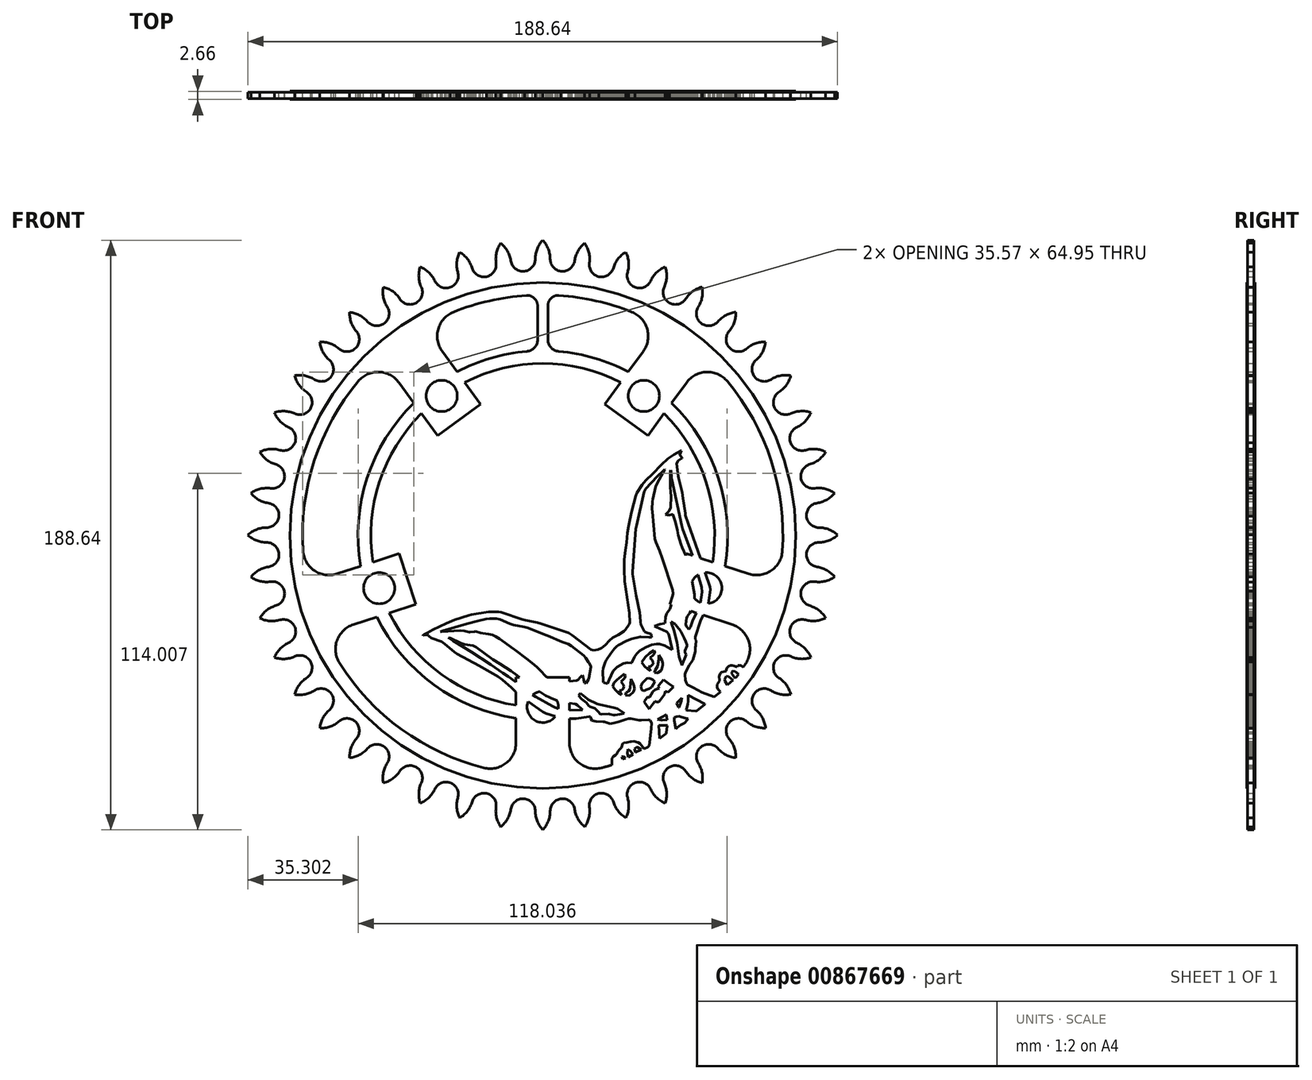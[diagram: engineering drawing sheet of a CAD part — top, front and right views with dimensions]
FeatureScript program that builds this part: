
annotation { "Feature Type Name" : "Feature", "Feature Type Description" : "" }
export const myFeature = defineFeature(function(context is Context, id is Id, definition is map)
    precondition{}
    {
        {
            var Q0;
            Q0=qCreatedBy(makeId("Front.planeOp"),FACE);
            var sketch = newSketch(context, id + "F0", { "sketchPlane" : qUnion([Q0])});
            skArc(sketch, "E0", {"start": v(-6.35, 84.36) * mm, "mid": v(-3.54, 85.52) * mm, "end": v(-2.38, 88.33) * mm});
            skArc(sketch, "E1.MirrorC", {"start": v(6.35, 84.36) * mm, "mid": v(3.54, 85.53) * mm, "end": v(2.38, 88.33) * mm});
            skPoint(sketch, "E2.orphan", {"position": v(12.57, 87.43) * mm});
            skPoint(sketch, "E3.trimOffspring.end.orphan", {"position": v(-12.57, 87.43) * mm});
            skLineSegment(sketch, "E4.trimOffspring", {"start": v(-5.78, 84.4) * mm, "end": v(-5.79, 84.4) * mm});
            skLineSegment(sketch, "E5.trimOffspring", {"start": v(5.78, 84.4) * mm, "end": v(5.79, 84.4) * mm});
            skPoint(sketch, "E6.MirrorCS.start.orphan", {"position": v(6.35, 0) * mm});
            skPoint(sketch, "E7.start.orphan", {"position": v(-6.35, 0) * mm});
            skArc(sketch, "E8.trimOffspring", {"start": v(-2.38, 88.33) * mm, "mid": v(-1.77, 91.55) * mm, "end": v(-0.01, 94.32) * mm});
            skPoint(sketch, "E9.trimOffspring.end.orphan", {"position": v(0, 88.33) * mm});
            skArc(sketch, "E10.trimOffspring", {"start": v(2.38, 88.33) * mm, "mid": v(1.76, 91.56) * mm, "end": v(-0.01, 94.32) * mm});
            skArc(sketch, "E11.1.0", {"start": v(-10.21, 87.77) * mm, "mid": v(-11.3, 90.88) * mm, "end": v(-13.44, 93.36) * mm});
            skPoint(sketch, "E11.1.2", {"position": v(-18.86, 86.53) * mm});
            skPoint(sketch, "E11.1.3", {"position": v(-6.29, 88.34) * mm});
            skArc(sketch, "E11.1.4", {"start": v(-14.93, 87.1) * mm, "mid": v(-14.78, 90.37) * mm, "end": v(-13.44, 93.36) * mm});
            skArc(sketch, "E11.1.5", {"start": v(-5.72, 84.4) * mm, "mid": v(-8.67, 85.16) * mm, "end": v(-10.21, 87.77) * mm});
            skArc(sketch, "E11.1.6", {"start": v(-18.3, 82.6) * mm, "mid": v(-15.68, 84.15) * mm, "end": v(-14.93, 87.1) * mm});
            skArc(sketch, "E11.2.0", {"start": v(-22.6, 85.43) * mm, "mid": v(-24.1, 88.34) * mm, "end": v(-26.59, 90.5) * mm});
            skPoint(sketch, "E11.2.1", {"position": v(-24.88, 84.75) * mm});
            skPoint(sketch, "E11.2.2", {"position": v(-30.98, 82.96) * mm});
            skPoint(sketch, "E11.2.3", {"position": v(-18.8, 86.54) * mm});
            skArc(sketch, "E11.2.4", {"start": v(-27.17, 84.08) * mm, "mid": v(-27.5, 87.35) * mm, "end": v(-26.59, 90.5) * mm});
            skArc(sketch, "E11.2.5", {"start": v(-17.67, 82.73) * mm, "mid": v(-20.7, 83.06) * mm, "end": v(-22.6, 85.43) * mm});
            skArc(sketch, "E11.2.6", {"start": v(-29.86, 79.16) * mm, "mid": v(-27.5, 81.06) * mm, "end": v(-27.17, 84.08) * mm});
            skArc(sketch, "E11.3.0", {"start": v(-34.53, 81.34) * mm, "mid": v(-36.43, 84.01) * mm, "end": v(-39.2, 85.8) * mm});
            skPoint(sketch, "E11.3.1", {"position": v(-36.7, 80.35) * mm});
            skPoint(sketch, "E11.3.2", {"position": v(-42.47, 77.71) * mm});
            skPoint(sketch, "E11.3.3", {"position": v(-30.92, 82.99) * mm});
            skArc(sketch, "E11.3.4", {"start": v(-38.86, 79.36) * mm, "mid": v(-39.64, 82.54) * mm, "end": v(-39.2, 85.8) * mm});
            skArc(sketch, "E11.3.5", {"start": v(-29.27, 79.38) * mm, "mid": v(-32.3, 79.27) * mm, "end": v(-34.53, 81.34) * mm});
            skArc(sketch, "E11.3.6", {"start": v(-40.82, 74.1) * mm, "mid": v(-38.75, 76.32) * mm, "end": v(-38.86, 79.36) * mm});
            skArc(sketch, "E11.4.0", {"start": v(-45.75, 75.6) * mm, "mid": v(-48.02, 77.97) * mm, "end": v(-51, 79.34) * mm});
            skPoint(sketch, "E11.4.1", {"position": v(-47.75, 74.3) * mm});
            skPoint(sketch, "E11.4.2", {"position": v(-53.1, 70.88) * mm});
            skPoint(sketch, "E11.4.3", {"position": v(-42.41, 77.74) * mm});
            skArc(sketch, "E11.4.4", {"start": v(-49.76, 73.02) * mm, "mid": v(-50.98, 76.06) * mm, "end": v(-51, 79.34) * mm});
            skArc(sketch, "E11.4.5", {"start": v(-40.27, 74.4) * mm, "mid": v(-43.26, 73.86) * mm, "end": v(-45.75, 75.6) * mm});
            skArc(sketch, "E11.4.6", {"start": v(-50.95, 67.54) * mm, "mid": v(-49.22, 70.03) * mm, "end": v(-49.76, 73.02) * mm});
            skArc(sketch, "E11.5.0", {"start": v(-56.05, 68.32) * mm, "mid": v(-58.63, 70.35) * mm, "end": v(-61.78, 71.28) * mm});
            skPoint(sketch, "E11.5.1", {"position": v(-57.84, 66.76) * mm});
            skPoint(sketch, "E11.5.2", {"position": v(-62.64, 62.6) * mm});
            skPoint(sketch, "E11.5.3", {"position": v(-53.04, 70.91) * mm});
            skArc(sketch, "E11.5.4", {"start": v(-59.64, 65.2) * mm, "mid": v(-61.29, 68.03) * mm, "end": v(-61.78, 71.28) * mm});
            skArc(sketch, "E11.5.5", {"start": v(-50.44, 67.92) * mm, "mid": v(-53.33, 66.96) * mm, "end": v(-56.05, 68.32) * mm});
            skArc(sketch, "E11.5.6", {"start": v(-60.04, 59.6) * mm, "mid": v(-58.68, 62.32) * mm, "end": v(-59.64, 65.2) * mm});
            skArc(sketch, "E11.6.0", {"start": v(-65.2, 59.65) * mm, "mid": v(-68.04, 61.29) * mm, "end": v(-71.3, 61.76) * mm});
            skPoint(sketch, "E11.6.1", {"position": v(-66.75, 57.85) * mm});
            skPoint(sketch, "E11.6.2", {"position": v(-70.91, 53.05) * mm});
            skPoint(sketch, "E11.6.3", {"position": v(-62.6, 62.64) * mm});
            skArc(sketch, "E11.6.4", {"start": v(-68.31, 56.05) * mm, "mid": v(-70.35, 58.62) * mm, "end": v(-71.3, 61.76) * mm});
            skArc(sketch, "E11.6.5", {"start": v(-59.6, 60.05) * mm, "mid": v(-62.31, 58.69) * mm, "end": v(-65.2, 59.65) * mm});
            skArc(sketch, "E11.6.6", {"start": v(-67.91, 50.45) * mm, "mid": v(-66.95, 53.33) * mm, "end": v(-68.31, 56.05) * mm});
            skArc(sketch, "E11.7.0", {"start": v(-73.02, 49.76) * mm, "mid": v(-76.07, 50.98) * mm, "end": v(-79.35, 50.99) * mm});
            skPoint(sketch, "E11.7.1", {"position": v(-74.3, 47.76) * mm});
            skPoint(sketch, "E11.7.2", {"position": v(-77.74, 42.42) * mm});
            skPoint(sketch, "E11.7.3", {"position": v(-70.87, 53.1) * mm});
            skArc(sketch, "E11.7.4", {"start": v(-75.6, 45.75) * mm, "mid": v(-77.97, 48.01) * mm, "end": v(-79.35, 50.99) * mm});
            skArc(sketch, "E11.7.5", {"start": v(-67.53, 50.95) * mm, "mid": v(-70.03, 49.22) * mm, "end": v(-73.02, 49.76) * mm});
            skArc(sketch, "E11.7.6", {"start": v(-74.4, 40.27) * mm, "mid": v(-73.86, 43.26) * mm, "end": v(-75.6, 45.75) * mm});
            skArc(sketch, "E11.8.0", {"start": v(-79.36, 38.86) * mm, "mid": v(-82.55, 39.63) * mm, "end": v(-85.8, 39.17) * mm});
            skPoint(sketch, "E11.8.1", {"position": v(-80.34, 36.7) * mm});
            skPoint(sketch, "E11.8.2", {"position": v(-82.98, 30.92) * mm});
            skPoint(sketch, "E11.8.3", {"position": v(-77.7, 42.47) * mm});
            skArc(sketch, "E11.8.4", {"start": v(-81.33, 34.53) * mm, "mid": v(-84.01, 36.42) * mm, "end": v(-85.8, 39.17) * mm});
            skArc(sketch, "E11.8.5", {"start": v(-74.1, 40.82) * mm, "mid": v(-76.32, 38.75) * mm, "end": v(-79.36, 38.86) * mm});
            skArc(sketch, "E11.8.6", {"start": v(-79.37, 29.27) * mm, "mid": v(-79.26, 32.3) * mm, "end": v(-81.33, 34.53) * mm});
            skArc(sketch, "E11.9.0", {"start": v(-84.08, 27.17) * mm, "mid": v(-87.35, 27.48) * mm, "end": v(-90.5, 26.56) * mm});
            skPoint(sketch, "E11.9.1", {"position": v(-84.75, 24.89) * mm});
            skPoint(sketch, "E11.9.2", {"position": v(-86.54, 18.8) * mm});
            skPoint(sketch, "E11.9.3", {"position": v(-82.96, 30.98) * mm});
            skArc(sketch, "E11.9.4", {"start": v(-85.42, 22.6) * mm, "mid": v(-88.34, 24.1) * mm, "end": v(-90.5, 26.56) * mm});
            skArc(sketch, "E11.9.5", {"start": v(-79.15, 29.86) * mm, "mid": v(-81.06, 27.5) * mm, "end": v(-84.08, 27.17) * mm});
            skArc(sketch, "E11.9.6", {"start": v(-82.73, 17.68) * mm, "mid": v(-83.05, 20.7) * mm, "end": v(-85.42, 22.6) * mm});
            skArc(sketch, "E11.10.0", {"start": v(-87.1, 14.93) * mm, "mid": v(-90.37, 14.77) * mm, "end": v(-93.36, 13.41) * mm});
            skPoint(sketch, "E11.10.1", {"position": v(-87.43, 12.57) * mm});
            skPoint(sketch, "E11.10.2", {"position": v(-88.33, 6.29) * mm});
            skPoint(sketch, "E11.10.3", {"position": v(-86.52, 18.86) * mm});
            skArc(sketch, "E11.10.4", {"start": v(-87.77, 10.22) * mm, "mid": v(-90.87, 11.28) * mm, "end": v(-93.36, 13.41) * mm});
            skArc(sketch, "E11.10.5", {"start": v(-82.6, 18.3) * mm, "mid": v(-84.15, 15.68) * mm, "end": v(-87.1, 14.93) * mm});
            skArc(sketch, "E11.10.6", {"start": v(-84.4, 5.72) * mm, "mid": v(-85.15, 8.67) * mm, "end": v(-87.77, 10.22) * mm});
            skArc(sketch, "E11.11.0", {"start": v(-88.33, 2.38) * mm, "mid": v(-91.55, 1.76) * mm, "end": v(-94.32, 0) * mm});
            skPoint(sketch, "E11.11.1", {"position": v(-88.33, 0) * mm});
            skPoint(sketch, "E11.11.2", {"position": v(-88.33, -6.35) * mm});
            skPoint(sketch, "E11.11.3", {"position": v(-88.33, 6.35) * mm});
            skArc(sketch, "E11.11.4", {"start": v(-88.33, -2.38) * mm, "mid": v(-91.55, -1.77) * mm, "end": v(-94.32, 0) * mm});
            skArc(sketch, "E11.11.5", {"start": v(-84.36, 6.35) * mm, "mid": v(-85.52, 3.55) * mm, "end": v(-88.33, 2.38) * mm});
            skArc(sketch, "E11.11.6", {"start": v(-84.36, -6.35) * mm, "mid": v(-85.52, -3.54) * mm, "end": v(-88.33, -2.38) * mm});
            skArc(sketch, "E11.12.0", {"start": v(-87.77, -10.21) * mm, "mid": v(-90.87, -11.29) * mm, "end": v(-93.36, -13.43) * mm});
            skPoint(sketch, "E11.12.1", {"position": v(-87.43, -12.57) * mm});
            skPoint(sketch, "E11.12.2", {"position": v(-86.52, -18.85) * mm});
            skPoint(sketch, "E11.12.3", {"position": v(-88.33, -6.28) * mm});
            skArc(sketch, "E11.12.4", {"start": v(-87.09, -14.92) * mm, "mid": v(-90.37, -14.78) * mm, "end": v(-93.36, -13.43) * mm});
            skArc(sketch, "E11.12.5", {"start": v(-84.4, -5.72) * mm, "mid": v(-85.16, -8.66) * mm, "end": v(-87.77, -10.21) * mm});
            skArc(sketch, "E11.12.6", {"start": v(-82.6, -18.29) * mm, "mid": v(-84.15, -15.67) * mm, "end": v(-87.09, -14.92) * mm});
            skArc(sketch, "E11.13.0", {"start": v(-85.42, -22.6) * mm, "mid": v(-88.34, -24.1) * mm, "end": v(-90.5, -26.58) * mm});
            skPoint(sketch, "E11.13.1", {"position": v(-84.75, -24.88) * mm});
            skPoint(sketch, "E11.13.2", {"position": v(-82.96, -30.97) * mm});
            skPoint(sketch, "E11.13.3", {"position": v(-86.54, -18.79) * mm});
            skArc(sketch, "E11.13.4", {"start": v(-84.08, -27.16) * mm, "mid": v(-87.34, -27.49) * mm, "end": v(-90.5, -26.58) * mm});
            skArc(sketch, "E11.13.5", {"start": v(-82.73, -17.67) * mm, "mid": v(-83.06, -20.7) * mm, "end": v(-85.42, -22.6) * mm});
            skArc(sketch, "E11.13.6", {"start": v(-79.15, -29.85) * mm, "mid": v(-81.06, -27.49) * mm, "end": v(-84.08, -27.16) * mm});
            skArc(sketch, "E11.14.0", {"start": v(-81.34, -34.52) * mm, "mid": v(-84.01, -36.43) * mm, "end": v(-85.8, -39.2) * mm});
            skPoint(sketch, "E11.14.1", {"position": v(-80.34, -36.69) * mm});
            skPoint(sketch, "E11.14.2", {"position": v(-77.7, -42.46) * mm});
            skPoint(sketch, "E11.14.3", {"position": v(-82.98, -30.91) * mm});
            skArc(sketch, "E11.14.4", {"start": v(-79.36, -38.85) * mm, "mid": v(-82.54, -39.64) * mm, "end": v(-85.8, -39.2) * mm});
            skArc(sketch, "E11.14.5", {"start": v(-79.37, -29.26) * mm, "mid": v(-79.26, -32.3) * mm, "end": v(-81.34, -34.52) * mm});
            skArc(sketch, "E11.14.6", {"start": v(-74.1, -40.82) * mm, "mid": v(-76.32, -38.75) * mm, "end": v(-79.36, -38.85) * mm});
            skArc(sketch, "E11.15.0", {"start": v(-75.6, -45.75) * mm, "mid": v(-77.97, -48.02) * mm, "end": v(-79.34, -51) * mm});
            skPoint(sketch, "E11.15.1", {"position": v(-74.3, -47.75) * mm});
            skPoint(sketch, "E11.15.2", {"position": v(-70.87, -53.1) * mm});
            skPoint(sketch, "E11.15.3", {"position": v(-77.74, -42.4) * mm});
            skArc(sketch, "E11.15.4", {"start": v(-73.02, -49.75) * mm, "mid": v(-76.06, -50.98) * mm, "end": v(-79.34, -51) * mm});
            skArc(sketch, "E11.15.5", {"start": v(-74.4, -40.26) * mm, "mid": v(-73.86, -43.25) * mm, "end": v(-75.6, -45.75) * mm});
            skArc(sketch, "E11.15.6", {"start": v(-67.53, -50.94) * mm, "mid": v(-70.03, -49.21) * mm, "end": v(-73.02, -49.75) * mm});
            skArc(sketch, "E11.16.0", {"start": v(-68.31, -56.04) * mm, "mid": v(-70.34, -58.62) * mm, "end": v(-71.27, -61.77) * mm});
            skPoint(sketch, "E11.16.1", {"position": v(-66.75, -57.84) * mm});
            skPoint(sketch, "E11.16.2", {"position": v(-62.6, -62.64) * mm});
            skPoint(sketch, "E11.16.3", {"position": v(-70.91, -53.04) * mm});
            skArc(sketch, "E11.16.4", {"start": v(-65.2, -59.64) * mm, "mid": v(-68.03, -61.29) * mm, "end": v(-71.27, -61.77) * mm});
            skArc(sketch, "E11.16.5", {"start": v(-67.91, -50.44) * mm, "mid": v(-66.95, -53.32) * mm, "end": v(-68.31, -56.04) * mm});
            skArc(sketch, "E11.16.6", {"start": v(-59.6, -60.04) * mm, "mid": v(-62.31, -58.68) * mm, "end": v(-65.2, -59.64) * mm});
            skArc(sketch, "E11.17.0", {"start": v(-59.64, -65.2) * mm, "mid": v(-61.28, -68.04) * mm, "end": v(-61.76, -71.29) * mm});
            skPoint(sketch, "E11.17.1", {"position": v(-57.84, -66.75) * mm});
            skPoint(sketch, "E11.17.2", {"position": v(-53.04, -70.9) * mm});
            skPoint(sketch, "E11.17.3", {"position": v(-62.64, -62.6) * mm});
            skArc(sketch, "E11.17.4", {"start": v(-56.04, -68.3) * mm, "mid": v(-58.61, -70.34) * mm, "end": v(-61.76, -71.29) * mm});
            skArc(sketch, "E11.17.5", {"start": v(-60.04, -59.6) * mm, "mid": v(-58.68, -62.3) * mm, "end": v(-59.64, -65.2) * mm});
            skArc(sketch, "E11.17.6", {"start": v(-50.44, -67.9) * mm, "mid": v(-53.33, -66.95) * mm, "end": v(-56.04, -68.3) * mm});
            skArc(sketch, "E11.18.0", {"start": v(-49.76, -73.02) * mm, "mid": v(-50.98, -76.07) * mm, "end": v(-50.98, -79.35) * mm});
            skPoint(sketch, "E11.18.1", {"position": v(-47.75, -74.3) * mm});
            skPoint(sketch, "E11.18.2", {"position": v(-42.41, -77.73) * mm});
            skPoint(sketch, "E11.18.3", {"position": v(-53.1, -70.87) * mm});
            skArc(sketch, "E11.18.4", {"start": v(-45.75, -75.59) * mm, "mid": v(-48, -77.97) * mm, "end": v(-50.98, -79.35) * mm});
            skArc(sketch, "E11.18.5", {"start": v(-50.95, -67.53) * mm, "mid": v(-49.22, -70.03) * mm, "end": v(-49.76, -73.02) * mm});
            skArc(sketch, "E11.18.6", {"start": v(-40.27, -74.4) * mm, "mid": v(-43.26, -73.86) * mm, "end": v(-45.75, -75.59) * mm});
            skArc(sketch, "E11.19.0", {"start": v(-38.86, -79.36) * mm, "mid": v(-39.63, -82.55) * mm, "end": v(-39.17, -85.8) * mm});
            skPoint(sketch, "E11.19.1", {"position": v(-36.7, -80.34) * mm});
            skPoint(sketch, "E11.19.2", {"position": v(-30.92, -82.98) * mm});
            skPoint(sketch, "E11.19.3", {"position": v(-42.47, -77.7) * mm});
            skArc(sketch, "E11.19.4", {"start": v(-34.53, -81.33) * mm, "mid": v(-36.42, -84) * mm, "end": v(-39.17, -85.8) * mm});
            skArc(sketch, "E11.19.5", {"start": v(-40.82, -74.1) * mm, "mid": v(-38.75, -76.32) * mm, "end": v(-38.86, -79.36) * mm});
            skArc(sketch, "E11.19.6", {"start": v(-29.27, -79.37) * mm, "mid": v(-32.3, -79.26) * mm, "end": v(-34.53, -81.33) * mm});
            skArc(sketch, "E11.20.0", {"start": v(-27.17, -84.08) * mm, "mid": v(-27.48, -87.35) * mm, "end": v(-26.56, -90.5) * mm});
            skPoint(sketch, "E11.20.1", {"position": v(-24.88, -84.74) * mm});
            skPoint(sketch, "E11.20.2", {"position": v(-18.8, -86.53) * mm});
            skPoint(sketch, "E11.20.3", {"position": v(-30.98, -82.96) * mm});
            skArc(sketch, "E11.20.4", {"start": v(-22.6, -85.42) * mm, "mid": v(-24.1, -88.34) * mm, "end": v(-26.56, -90.5) * mm});
            skArc(sketch, "E11.20.5", {"start": v(-29.86, -79.15) * mm, "mid": v(-27.5, -81.06) * mm, "end": v(-27.17, -84.08) * mm});
            skArc(sketch, "E11.20.6", {"start": v(-17.67, -82.73) * mm, "mid": v(-20.7, -83.05) * mm, "end": v(-22.6, -85.42) * mm});
            skArc(sketch, "E11.21.0", {"start": v(-14.93, -87.09) * mm, "mid": v(-14.77, -90.37) * mm, "end": v(-13.4, -93.36) * mm});
            skPoint(sketch, "E11.21.1", {"position": v(-12.57, -87.42) * mm});
            skPoint(sketch, "E11.21.2", {"position": v(-6.29, -88.33) * mm});
            skPoint(sketch, "E11.21.3", {"position": v(-18.86, -86.52) * mm});
            skArc(sketch, "E11.21.4", {"start": v(-10.21, -87.76) * mm, "mid": v(-11.28, -90.87) * mm, "end": v(-13.4, -93.36) * mm});
            skArc(sketch, "E11.21.5", {"start": v(-18.3, -82.6) * mm, "mid": v(-15.68, -84.14) * mm, "end": v(-14.93, -87.09) * mm});
            skArc(sketch, "E11.21.6", {"start": v(-5.72, -84.4) * mm, "mid": v(-8.66, -85.15) * mm, "end": v(-10.21, -87.76) * mm});
            skArc(sketch, "E11.22.0", {"start": v(-2.38, -88.33) * mm, "mid": v(-1.76, -91.55) * mm, "end": v(0.01, -94.32) * mm});
            skPoint(sketch, "E11.22.1", {"position": v(0, -88.32) * mm});
            skPoint(sketch, "E11.22.2", {"position": v(6.35, -88.32) * mm});
            skPoint(sketch, "E11.22.3", {"position": v(-6.35, -88.32) * mm});
            skArc(sketch, "E11.22.4", {"start": v(2.38, -88.32) * mm, "mid": v(1.77, -91.55) * mm, "end": v(0.01, -94.32) * mm});
            skArc(sketch, "E11.22.5", {"start": v(-6.35, -84.35) * mm, "mid": v(-3.54, -85.52) * mm, "end": v(-2.38, -88.33) * mm});
            skArc(sketch, "E11.22.6", {"start": v(6.35, -84.35) * mm, "mid": v(3.54, -85.52) * mm, "end": v(2.38, -88.32) * mm});
            skArc(sketch, "E11.23.0", {"start": v(10.21, -87.77) * mm, "mid": v(11.3, -90.87) * mm, "end": v(13.44, -93.35) * mm});
            skPoint(sketch, "E11.23.1", {"position": v(12.57, -87.42) * mm});
            skPoint(sketch, "E11.23.2", {"position": v(18.86, -86.52) * mm});
            skPoint(sketch, "E11.23.3", {"position": v(6.29, -88.33) * mm});
            skArc(sketch, "E11.23.4", {"start": v(14.93, -87.08) * mm, "mid": v(14.78, -90.36) * mm, "end": v(13.44, -93.35) * mm});
            skArc(sketch, "E11.23.5", {"start": v(5.72, -84.4) * mm, "mid": v(8.67, -85.15) * mm, "end": v(10.21, -87.77) * mm});
            skArc(sketch, "E11.23.6", {"start": v(18.3, -82.6) * mm, "mid": v(15.68, -84.14) * mm, "end": v(14.93, -87.08) * mm});
            skArc(sketch, "E11.24.0", {"start": v(22.6, -85.42) * mm, "mid": v(24.1, -88.34) * mm, "end": v(26.59, -90.5) * mm});
            skPoint(sketch, "E11.24.1", {"position": v(24.88, -84.74) * mm});
            skPoint(sketch, "E11.24.2", {"position": v(30.98, -82.96) * mm});
            skPoint(sketch, "E11.24.3", {"position": v(18.8, -86.53) * mm});
            skArc(sketch, "E11.24.4", {"start": v(27.17, -84.07) * mm, "mid": v(27.5, -87.34) * mm, "end": v(26.59, -90.5) * mm});
            skArc(sketch, "E11.24.5", {"start": v(17.67, -82.73) * mm, "mid": v(20.7, -83.05) * mm, "end": v(22.6, -85.42) * mm});
            skArc(sketch, "E11.24.6", {"start": v(29.86, -79.15) * mm, "mid": v(27.5, -81.05) * mm, "end": v(27.17, -84.07) * mm});
            skArc(sketch, "E11.25.0", {"start": v(34.53, -81.33) * mm, "mid": v(36.43, -84) * mm, "end": v(39.2, -85.79) * mm});
            skPoint(sketch, "E11.25.1", {"position": v(36.7, -80.34) * mm});
            skPoint(sketch, "E11.25.2", {"position": v(42.47, -77.7) * mm});
            skPoint(sketch, "E11.25.3", {"position": v(30.92, -82.98) * mm});
            skArc(sketch, "E11.25.4", {"start": v(38.86, -79.35) * mm, "mid": v(39.64, -82.54) * mm, "end": v(39.2, -85.79) * mm});
            skArc(sketch, "E11.25.5", {"start": v(29.27, -79.37) * mm, "mid": v(32.3, -79.26) * mm, "end": v(34.53, -81.33) * mm});
            skArc(sketch, "E11.25.6", {"start": v(40.82, -74.1) * mm, "mid": v(38.75, -76.32) * mm, "end": v(38.86, -79.35) * mm});
            skArc(sketch, "E11.26.0", {"start": v(45.75, -75.6) * mm, "mid": v(48.02, -77.97) * mm, "end": v(51, -79.34) * mm});
            skPoint(sketch, "E11.26.1", {"position": v(47.75, -74.3) * mm});
            skPoint(sketch, "E11.26.2", {"position": v(53.1, -70.87) * mm});
            skPoint(sketch, "E11.26.3", {"position": v(42.41, -77.73) * mm});
            skArc(sketch, "E11.26.4", {"start": v(49.76, -73.01) * mm, "mid": v(50.98, -76.06) * mm, "end": v(51, -79.34) * mm});
            skArc(sketch, "E11.26.5", {"start": v(40.27, -74.4) * mm, "mid": v(43.26, -73.86) * mm, "end": v(45.75, -75.6) * mm});
            skArc(sketch, "E11.26.6", {"start": v(50.95, -67.53) * mm, "mid": v(49.22, -70.02) * mm, "end": v(49.76, -73.01) * mm});
            skArc(sketch, "E11.27.0", {"start": v(56.05, -68.31) * mm, "mid": v(58.63, -70.34) * mm, "end": v(61.78, -71.27) * mm});
            skPoint(sketch, "E11.27.1", {"position": v(57.84, -66.75) * mm});
            skPoint(sketch, "E11.27.2", {"position": v(62.64, -62.6) * mm});
            skPoint(sketch, "E11.27.3", {"position": v(53.04, -70.9) * mm});
            skArc(sketch, "E11.27.4", {"start": v(59.64, -65.19) * mm, "mid": v(61.29, -68.03) * mm, "end": v(61.78, -71.27) * mm});
            skArc(sketch, "E11.27.5", {"start": v(50.44, -67.9) * mm, "mid": v(53.33, -66.95) * mm, "end": v(56.05, -68.31) * mm});
            skArc(sketch, "E11.27.6", {"start": v(60.04, -59.6) * mm, "mid": v(58.68, -62.3) * mm, "end": v(59.64, -65.19) * mm});
            skArc(sketch, "E11.28.0", {"start": v(65.2, -59.64) * mm, "mid": v(68.04, -61.28) * mm, "end": v(71.3, -61.75) * mm});
            skPoint(sketch, "E11.28.1", {"position": v(66.75, -57.84) * mm});
            skPoint(sketch, "E11.28.2", {"position": v(70.91, -53.04) * mm});
            skPoint(sketch, "E11.28.3", {"position": v(62.6, -62.64) * mm});
            skArc(sketch, "E11.28.4", {"start": v(68.31, -56.04) * mm, "mid": v(70.35, -58.61) * mm, "end": v(71.3, -61.75) * mm});
            skArc(sketch, "E11.28.5", {"start": v(59.6, -60.04) * mm, "mid": v(62.31, -58.68) * mm, "end": v(65.2, -59.64) * mm});
            skArc(sketch, "E11.28.6", {"start": v(67.91, -50.44) * mm, "mid": v(66.95, -53.32) * mm, "end": v(68.31, -56.04) * mm});
            skArc(sketch, "E11.29.0", {"start": v(73.02, -49.75) * mm, "mid": v(76.07, -50.97) * mm, "end": v(79.35, -50.98) * mm});
            skPoint(sketch, "E11.29.1", {"position": v(74.3, -47.75) * mm});
            skPoint(sketch, "E11.29.2", {"position": v(77.74, -42.4) * mm});
            skPoint(sketch, "E11.29.3", {"position": v(70.87, -53.1) * mm});
            skArc(sketch, "E11.29.4", {"start": v(75.6, -45.75) * mm, "mid": v(77.97, -48) * mm, "end": v(79.35, -50.98) * mm});
            skArc(sketch, "E11.29.5", {"start": v(67.53, -50.94) * mm, "mid": v(70.03, -49.21) * mm, "end": v(73.02, -49.75) * mm});
            skArc(sketch, "E11.29.6", {"start": v(74.4, -40.26) * mm, "mid": v(73.86, -43.25) * mm, "end": v(75.6, -45.75) * mm});
            skArc(sketch, "E11.30.0", {"start": v(79.36, -38.86) * mm, "mid": v(82.55, -39.63) * mm, "end": v(85.8, -39.17) * mm});
            skPoint(sketch, "E11.30.1", {"position": v(80.34, -36.69) * mm});
            skPoint(sketch, "E11.30.2", {"position": v(82.98, -30.91) * mm});
            skPoint(sketch, "E11.30.3", {"position": v(77.7, -42.46) * mm});
            skArc(sketch, "E11.30.4", {"start": v(81.33, -34.52) * mm, "mid": v(84.01, -36.42) * mm, "end": v(85.8, -39.17) * mm});
            skArc(sketch, "E11.30.5", {"start": v(74.1, -40.82) * mm, "mid": v(76.32, -38.74) * mm, "end": v(79.36, -38.86) * mm});
            skArc(sketch, "E11.30.6", {"start": v(79.37, -29.26) * mm, "mid": v(79.26, -32.3) * mm, "end": v(81.33, -34.52) * mm});
            skArc(sketch, "E11.31.0", {"start": v(84.08, -27.17) * mm, "mid": v(87.35, -27.48) * mm, "end": v(90.5, -26.56) * mm});
            skPoint(sketch, "E11.31.1", {"position": v(84.75, -24.88) * mm});
            skPoint(sketch, "E11.31.2", {"position": v(86.54, -18.79) * mm});
            skPoint(sketch, "E11.31.3", {"position": v(82.96, -30.97) * mm});
            skArc(sketch, "E11.31.4", {"start": v(85.42, -22.6) * mm, "mid": v(88.34, -24.1) * mm, "end": v(90.5, -26.56) * mm});
            skArc(sketch, "E11.31.5", {"start": v(79.15, -29.85) * mm, "mid": v(81.06, -27.49) * mm, "end": v(84.08, -27.17) * mm});
            skArc(sketch, "E11.31.6", {"start": v(82.73, -17.67) * mm, "mid": v(83.05, -20.7) * mm, "end": v(85.42, -22.6) * mm});
            skArc(sketch, "E11.32.0", {"start": v(87.1, -14.92) * mm, "mid": v(90.37, -14.76) * mm, "end": v(93.36, -13.4) * mm});
            skPoint(sketch, "E11.32.1", {"position": v(87.43, -12.57) * mm});
            skPoint(sketch, "E11.32.2", {"position": v(88.33, -6.28) * mm});
            skPoint(sketch, "E11.32.3", {"position": v(86.52, -18.85) * mm});
            skArc(sketch, "E11.32.4", {"start": v(87.77, -10.2) * mm, "mid": v(90.87, -11.27) * mm, "end": v(93.36, -13.4) * mm});
            skArc(sketch, "E11.32.5", {"start": v(82.6, -18.29) * mm, "mid": v(84.15, -15.67) * mm, "end": v(87.1, -14.92) * mm});
            skArc(sketch, "E11.32.6", {"start": v(84.4, -5.72) * mm, "mid": v(85.15, -8.66) * mm, "end": v(87.77, -10.2) * mm});
            skArc(sketch, "E11.33.0", {"start": v(88.33, -2.38) * mm, "mid": v(91.55, -1.75) * mm, "end": v(94.32, 0.02) * mm});
            skPoint(sketch, "E11.33.1", {"position": v(88.33, 0) * mm});
            skPoint(sketch, "E11.33.2", {"position": v(88.33, 6.35) * mm});
            skPoint(sketch, "E11.33.3", {"position": v(88.33, -6.35) * mm});
            skArc(sketch, "E11.33.4", {"start": v(88.33, 2.38) * mm, "mid": v(91.55, 1.77) * mm, "end": v(94.32, 0.02) * mm});
            skArc(sketch, "E11.33.5", {"start": v(84.36, -6.35) * mm, "mid": v(85.52, -3.54) * mm, "end": v(88.33, -2.38) * mm});
            skArc(sketch, "E11.33.6", {"start": v(84.36, 6.35) * mm, "mid": v(85.52, 3.55) * mm, "end": v(88.33, 2.38) * mm});
            skArc(sketch, "E11.34.0", {"start": v(87.77, 10.22) * mm, "mid": v(90.87, 11.3) * mm, "end": v(93.36, 13.44) * mm});
            skPoint(sketch, "E11.34.1", {"position": v(87.43, 12.57) * mm});
            skPoint(sketch, "E11.34.2", {"position": v(86.52, 18.86) * mm});
            skPoint(sketch, "E11.34.3", {"position": v(88.33, 6.29) * mm});
            skArc(sketch, "E11.34.4", {"start": v(87.09, 14.93) * mm, "mid": v(90.37, 14.78) * mm, "end": v(93.36, 13.44) * mm});
            skArc(sketch, "E11.34.5", {"start": v(84.4, 5.72) * mm, "mid": v(85.16, 8.67) * mm, "end": v(87.77, 10.22) * mm});
            skArc(sketch, "E11.34.6", {"start": v(82.6, 18.3) * mm, "mid": v(84.15, 15.68) * mm, "end": v(87.09, 14.93) * mm});
            skArc(sketch, "E11.35.0", {"start": v(85.42, 22.6) * mm, "mid": v(88.34, 24.11) * mm, "end": v(90.5, 26.59) * mm});
            skPoint(sketch, "E11.35.1", {"position": v(84.75, 24.89) * mm});
            skPoint(sketch, "E11.35.2", {"position": v(82.96, 30.98) * mm});
            skPoint(sketch, "E11.35.3", {"position": v(86.54, 18.8) * mm});
            skArc(sketch, "E11.35.4", {"start": v(84.08, 27.17) * mm, "mid": v(87.34, 27.5) * mm, "end": v(90.5, 26.59) * mm});
            skArc(sketch, "E11.35.5", {"start": v(82.73, 17.68) * mm, "mid": v(83.06, 20.7) * mm, "end": v(85.42, 22.6) * mm});
            skArc(sketch, "E11.35.6", {"start": v(79.15, 29.86) * mm, "mid": v(81.06, 27.5) * mm, "end": v(84.08, 27.17) * mm});
            skArc(sketch, "E11.36.0", {"start": v(81.34, 34.53) * mm, "mid": v(84.01, 36.44) * mm, "end": v(85.8, 39.2) * mm});
            skPoint(sketch, "E11.36.1", {"position": v(80.34, 36.7) * mm});
            skPoint(sketch, "E11.36.2", {"position": v(77.7, 42.47) * mm});
            skPoint(sketch, "E11.36.3", {"position": v(82.98, 30.92) * mm});
            skArc(sketch, "E11.36.4", {"start": v(79.36, 38.86) * mm, "mid": v(82.54, 39.64) * mm, "end": v(85.8, 39.2) * mm});
            skArc(sketch, "E11.36.5", {"start": v(79.37, 29.27) * mm, "mid": v(79.26, 32.3) * mm, "end": v(81.34, 34.53) * mm});
            skArc(sketch, "E11.36.6", {"start": v(74.1, 40.82) * mm, "mid": v(76.32, 38.75) * mm, "end": v(79.36, 38.86) * mm});
            skArc(sketch, "E11.37.0", {"start": v(75.6, 45.76) * mm, "mid": v(77.97, 48.02) * mm, "end": v(79.34, 51) * mm});
            skPoint(sketch, "E11.37.1", {"position": v(74.3, 47.76) * mm});
            skPoint(sketch, "E11.37.2", {"position": v(70.87, 53.1) * mm});
            skPoint(sketch, "E11.37.3", {"position": v(77.74, 42.42) * mm});
            skArc(sketch, "E11.37.4", {"start": v(73.02, 49.76) * mm, "mid": v(76.06, 50.99) * mm, "end": v(79.34, 51) * mm});
            skArc(sketch, "E11.37.5", {"start": v(74.4, 40.27) * mm, "mid": v(73.86, 43.26) * mm, "end": v(75.6, 45.76) * mm});
            skArc(sketch, "E11.37.6", {"start": v(67.53, 50.95) * mm, "mid": v(70.03, 49.22) * mm, "end": v(73.02, 49.76) * mm});
            skArc(sketch, "E11.38.0", {"start": v(68.31, 56.05) * mm, "mid": v(70.34, 58.63) * mm, "end": v(71.27, 61.78) * mm});
            skPoint(sketch, "E11.38.1", {"position": v(66.75, 57.85) * mm});
            skPoint(sketch, "E11.38.2", {"position": v(62.6, 62.64) * mm});
            skPoint(sketch, "E11.38.3", {"position": v(70.91, 53.05) * mm});
            skArc(sketch, "E11.38.4", {"start": v(65.2, 59.64) * mm, "mid": v(68.03, 61.3) * mm, "end": v(71.27, 61.78) * mm});
            skArc(sketch, "E11.38.5", {"start": v(67.91, 50.45) * mm, "mid": v(66.95, 53.33) * mm, "end": v(68.31, 56.05) * mm});
            skArc(sketch, "E11.38.6", {"start": v(59.6, 60.05) * mm, "mid": v(62.31, 58.69) * mm, "end": v(65.2, 59.64) * mm});
            skArc(sketch, "E11.39.0", {"start": v(59.64, 65.2) * mm, "mid": v(61.28, 68.05) * mm, "end": v(61.76, 71.3) * mm});
            skPoint(sketch, "E11.39.1", {"position": v(57.84, 66.76) * mm});
            skPoint(sketch, "E11.39.2", {"position": v(53.04, 70.91) * mm});
            skPoint(sketch, "E11.39.3", {"position": v(62.64, 62.6) * mm});
            skArc(sketch, "E11.39.4", {"start": v(56.04, 68.32) * mm, "mid": v(58.61, 70.35) * mm, "end": v(61.76, 71.3) * mm});
            skArc(sketch, "E11.39.5", {"start": v(60.04, 59.6) * mm, "mid": v(58.68, 62.32) * mm, "end": v(59.64, 65.2) * mm});
            skArc(sketch, "E11.39.6", {"start": v(50.44, 67.92) * mm, "mid": v(53.33, 66.96) * mm, "end": v(56.04, 68.32) * mm});
            skArc(sketch, "E11.40.0", {"start": v(49.76, 73.03) * mm, "mid": v(50.98, 76.07) * mm, "end": v(50.98, 79.36) * mm});
            skPoint(sketch, "E11.40.1", {"position": v(47.75, 74.3) * mm});
            skPoint(sketch, "E11.40.2", {"position": v(42.41, 77.74) * mm});
            skPoint(sketch, "E11.40.3", {"position": v(53.1, 70.88) * mm});
            skArc(sketch, "E11.40.4", {"start": v(45.75, 75.6) * mm, "mid": v(48, 77.98) * mm, "end": v(50.98, 79.36) * mm});
            skArc(sketch, "E11.40.5", {"start": v(50.95, 67.54) * mm, "mid": v(49.22, 70.03) * mm, "end": v(49.76, 73.03) * mm});
            skArc(sketch, "E11.40.6", {"start": v(40.27, 74.4) * mm, "mid": v(43.26, 73.86) * mm, "end": v(45.75, 75.6) * mm});
            skArc(sketch, "E11.41.0", {"start": v(38.86, 79.36) * mm, "mid": v(39.63, 82.55) * mm, "end": v(39.17, 85.8) * mm});
            skPoint(sketch, "E11.41.1", {"position": v(36.7, 80.35) * mm});
            skPoint(sketch, "E11.41.2", {"position": v(30.92, 82.99) * mm});
            skPoint(sketch, "E11.41.3", {"position": v(42.47, 77.71) * mm});
            skArc(sketch, "E11.41.4", {"start": v(34.53, 81.34) * mm, "mid": v(36.42, 84.02) * mm, "end": v(39.17, 85.8) * mm});
            skArc(sketch, "E11.41.5", {"start": v(40.82, 74.1) * mm, "mid": v(38.75, 76.33) * mm, "end": v(38.86, 79.36) * mm});
            skArc(sketch, "E11.41.6", {"start": v(29.27, 79.38) * mm, "mid": v(32.3, 79.27) * mm, "end": v(34.53, 81.34) * mm});
            skArc(sketch, "E11.42.0", {"start": v(27.17, 84.09) * mm, "mid": v(27.48, 87.35) * mm, "end": v(26.56, 90.5) * mm});
            skPoint(sketch, "E11.42.1", {"position": v(24.88, 84.75) * mm});
            skPoint(sketch, "E11.42.2", {"position": v(18.8, 86.54) * mm});
            skPoint(sketch, "E11.42.3", {"position": v(30.98, 82.96) * mm});
            skArc(sketch, "E11.42.4", {"start": v(22.6, 85.42) * mm, "mid": v(24.1, 88.34) * mm, "end": v(26.56, 90.5) * mm});
            skArc(sketch, "E11.42.5", {"start": v(29.86, 79.16) * mm, "mid": v(27.5, 81.06) * mm, "end": v(27.17, 84.09) * mm});
            skArc(sketch, "E11.42.6", {"start": v(17.67, 82.73) * mm, "mid": v(20.7, 83.06) * mm, "end": v(22.6, 85.42) * mm});
            skArc(sketch, "E11.43.0", {"start": v(14.93, 87.1) * mm, "mid": v(14.77, 90.38) * mm, "end": v(13.4, 93.37) * mm});
            skPoint(sketch, "E11.43.2", {"position": v(6.29, 88.34) * mm});
            skPoint(sketch, "E11.43.3", {"position": v(18.86, 86.53) * mm});
            skArc(sketch, "E11.43.4", {"start": v(10.21, 87.77) * mm, "mid": v(11.28, 90.87) * mm, "end": v(13.4, 93.37) * mm});
            skArc(sketch, "E11.43.5", {"start": v(18.3, 82.6) * mm, "mid": v(15.68, 84.15) * mm, "end": v(14.93, 87.1) * mm});
            skArc(sketch, "E11.43.6", {"start": v(5.72, 84.4) * mm, "mid": v(8.66, 85.16) * mm, "end": v(10.21, 87.77) * mm});
            skPoint(sketch, "E11.center", {"position": v(0, 0) * mm});
            skCircle(sketch, "E12", {"center": v(0, 0) * mm, "radius": 76.83 * mm});
            skCircle(sketch, "E13", {"center": v(0, 0) * mm, "radius": 55 * mm, "construction": true});
            skPoint(sketch, "E14.visualSharp", {"position": v(-8.57, -72.7) * mm});
            skPoint(sketch, "E15.visualSharp", {"position": v(8.57, -72.7) * mm});
            skCircle(sketch, "E16", {"center": v(0, -55) * mm, "radius": 5 * mm});
            skLineSegment(sketch, "E17", {"start": v(-8.54, -45.5) * mm, "end": v(-8.54, -66.46) * mm});
            skArc(sketch, "E18", {"start": v(-18.85, -74.48) * mm, "mid": v(-11.73, -72.99) * mm, "end": v(-8.54, -66.46) * mm});
            skLineSegment(sketch, "E19", {"start": v(-8.54, -45.5) * mm, "end": v(0, -45.5) * mm});
            skLineSegment(sketch, "E20.MirrorCS", {"start": v(8.54, -45.5) * mm, "end": v(8.54, -66.46) * mm});
            skLineSegment(sketch, "E21.MirrorCS", {"start": v(8.54, -45.5) * mm, "end": v(0, -45.5) * mm});
            skArc(sketch, "E22.MirrorCS", {"start": v(18.85, -74.48) * mm, "mid": v(11.73, -72.99) * mm, "end": v(8.54, -66.46) * mm});
            skPoint(sketch, "E23.center", {"position": v(0, -0.14) * mm});
            skArc(sketch, "E24.1.0", {"start": v(65.02, -40.94) * mm, "mid": v(65.8, -33.71) * mm, "end": v(60.57, -28.65) * mm});
            skLineSegment(sketch, "E24.1.1", {"start": v(40.64, -22.18) * mm, "end": v(60.57, -28.65) * mm});
            skLineSegment(sketch, "E24.1.2", {"start": v(40.64, -22.18) * mm, "end": v(43.28, -14.06) * mm});
            skLineSegment(sketch, "E24.1.3", {"start": v(45.92, -5.94) * mm, "end": v(43.28, -14.06) * mm});
            skLineSegment(sketch, "E24.1.4", {"start": v(45.92, -5.94) * mm, "end": v(65.85, -12.41) * mm});
            skArc(sketch, "E24.1.5", {"start": v(76.67, -5.09) * mm, "mid": v(73.05, -11.4) * mm, "end": v(65.85, -12.41) * mm});
            skCircle(sketch, "E24.1.6", {"center": v(52.3, -17) * mm, "radius": 5 * mm});
            skArc(sketch, "E24.2.0", {"start": v(59.03, 49.19) * mm, "mid": v(52.4, 52.16) * mm, "end": v(45.97, 48.75) * mm});
            skLineSegment(sketch, "E24.2.1", {"start": v(33.66, 31.8) * mm, "end": v(45.97, 48.75) * mm});
            skLineSegment(sketch, "E24.2.2", {"start": v(33.66, 31.8) * mm, "end": v(26.75, 36.82) * mm});
            skLineSegment(sketch, "E24.2.3", {"start": v(19.84, 41.84) * mm, "end": v(26.75, 36.82) * mm});
            skLineSegment(sketch, "E24.2.4", {"start": v(19.84, 41.84) * mm, "end": v(32.16, 58.8) * mm});
            skArc(sketch, "E24.2.5", {"start": v(28.53, 71.34) * mm, "mid": v(33.41, 65.95) * mm, "end": v(32.16, 58.8) * mm});
            skCircle(sketch, "E24.2.6", {"center": v(32.33, 44.5) * mm, "radius": 5 * mm});
            skArc(sketch, "E24.3.0", {"start": v(-28.53, 71.34) * mm, "mid": v(-33.41, 65.95) * mm, "end": v(-32.16, 58.8) * mm});
            skLineSegment(sketch, "E24.3.1", {"start": v(-19.84, 41.84) * mm, "end": v(-32.16, 58.8) * mm});
            skLineSegment(sketch, "E24.3.2", {"start": v(-19.84, 41.84) * mm, "end": v(-26.75, 36.82) * mm});
            skLineSegment(sketch, "E24.3.3", {"start": v(-33.66, 31.8) * mm, "end": v(-26.75, 36.82) * mm});
            skLineSegment(sketch, "E24.3.4", {"start": v(-33.66, 31.8) * mm, "end": v(-45.97, 48.75) * mm});
            skArc(sketch, "E24.3.5", {"start": v(-59.03, 49.19) * mm, "mid": v(-52.4, 52.16) * mm, "end": v(-45.97, 48.75) * mm});
            skCircle(sketch, "E24.3.6", {"center": v(-32.33, 44.5) * mm, "radius": 5 * mm});
            skArc(sketch, "E24.4.0", {"start": v(-76.67, -5.09) * mm, "mid": v(-73.05, -11.4) * mm, "end": v(-65.85, -12.41) * mm});
            skLineSegment(sketch, "E24.4.1", {"start": v(-45.92, -5.94) * mm, "end": v(-65.85, -12.41) * mm});
            skLineSegment(sketch, "E24.4.2", {"start": v(-45.92, -5.94) * mm, "end": v(-43.28, -14.06) * mm});
            skLineSegment(sketch, "E24.4.3", {"start": v(-40.64, -22.18) * mm, "end": v(-43.28, -14.06) * mm});
            skLineSegment(sketch, "E24.4.4", {"start": v(-40.64, -22.18) * mm, "end": v(-60.57, -28.65) * mm});
            skArc(sketch, "E24.4.5", {"start": v(-65.02, -40.94) * mm, "mid": v(-65.8, -33.71) * mm, "end": v(-60.57, -28.65) * mm});
            skCircle(sketch, "E24.4.6", {"center": v(-52.3, -17) * mm, "radius": 5 * mm});
            skCircle(sketch, "E25", {"center": v(0, -0.14) * mm, "radius": 80.91 * mm});
            skCircle(sketch, "E26", {"center": v(0, -0.14) * mm, "radius": 55 * mm});
            skCircle(sketch, "E27", {"center": v(0, -0.14) * mm, "radius": 59.12 * mm});
            skLineSegment(sketch, "E28", {"start": v(-1.65, 73.38) * mm, "end": v(-1.65, 62.51) * mm});
            skArc(sketch, "E29", {"start": v(-1.65, 73.38) * mm, "mid": v(-2.7, 75.78) * mm, "end": v(-5.17, 76.66) * mm});
            skArc(sketch, "E30", {"start": v(-5.09, 58.76) * mm, "mid": v(-2.64, 59.97) * mm, "end": v(-1.65, 62.51) * mm});
            skArc(sketch, "E31.MirrorCS", {"start": v(1.65, 73.38) * mm, "mid": v(2.7, 75.78) * mm, "end": v(5.17, 76.66) * mm});
            skLineSegment(sketch, "E32.MirrorCS", {"start": v(1.65, 73.38) * mm, "end": v(1.65, 62.51) * mm});
            skArc(sketch, "E33.MirrorCS", {"start": v(5.09, 58.76) * mm, "mid": v(2.64, 59.97) * mm, "end": v(1.65, 62.51) * mm});
            skSolve(sketch);
        }
        {
            var Q0;
            Q0=qCreatedBy(makeId("Front.planeOp"),FACE);
            var sketch = newSketch(context, id + "F1", { "sketchPlane" : qUnion([Q0])});
            skLineSegment(sketch, "E34", {"start": v(47.58, -60.9) * mm, "end": v(46.68, -61.57) * mm});
            skLineSegment(sketch, "E35", {"start": v(46.68, -61.57) * mm, "end": v(46.33, -61.77) * mm});
            skLineSegment(sketch, "E36", {"start": v(46.33, -61.77) * mm, "end": v(44.46, -63.07) * mm});
            skLineSegment(sketch, "E37", {"start": v(44.46, -63.07) * mm, "end": v(39.14, -66.77) * mm});
            skLineSegment(sketch, "E38", {"start": v(39.14, -66.77) * mm, "end": v(35.3, -69.16) * mm});
            skLineSegment(sketch, "E39", {"start": v(35.3, -69.16) * mm, "end": v(31.9, -71.04) * mm});
            skLineSegment(sketch, "E40", {"start": v(31.9, -71.04) * mm, "end": v(30.35, -71.84) * mm});
            skLineSegment(sketch, "E41", {"start": v(30.35, -71.84) * mm, "end": v(22.34, -75.3) * mm});
            skLineSegment(sketch, "E42", {"start": v(22.34, -75.3) * mm, "end": v(22.17, -75.35) * mm});
            skLineSegment(sketch, "E43", {"start": v(22.17, -75.35) * mm, "end": v(22.07, -74.58) * mm});
            skLineSegment(sketch, "E44", {"start": v(22.07, -74.58) * mm, "end": v(22.07, -71.72) * mm});
            skLineSegment(sketch, "E45", {"start": v(22.07, -71.72) * mm, "end": v(22.12, -71.47) * mm});
            skLineSegment(sketch, "E46", {"start": v(22.12, -71.47) * mm, "end": v(22.61, -70.76) * mm});
            skLineSegment(sketch, "E47", {"start": v(22.61, -70.76) * mm, "end": v(23.29, -70.38) * mm});
            skLineSegment(sketch, "E48", {"start": v(23.29, -70.38) * mm, "end": v(23.76, -69.94) * mm});
            skLineSegment(sketch, "E49", {"start": v(23.76, -69.94) * mm, "end": v(23.92, -69.44) * mm});
            skLineSegment(sketch, "E50", {"start": v(23.92, -69.44) * mm, "end": v(24.68, -68.57) * mm});
            skLineSegment(sketch, "E51", {"start": v(24.68, -68.57) * mm, "end": v(25.2, -67.95) * mm});
            skLineSegment(sketch, "E52", {"start": v(25.2, -67.95) * mm, "end": v(25.53, -66.79) * mm});
            skLineSegment(sketch, "E53", {"start": v(25.53, -66.79) * mm, "end": v(25.9, -66.47) * mm});
            skLineSegment(sketch, "E54", {"start": v(25.9, -66.47) * mm, "end": v(26.95, -66.36) * mm});
            skLineSegment(sketch, "E55", {"start": v(26.95, -66.36) * mm, "end": v(28.16, -66.12) * mm});
            skLineSegment(sketch, "E56", {"start": v(28.16, -66.12) * mm, "end": v(28.4, -66.05) * mm});
            skLineSegment(sketch, "E57", {"start": v(28.4, -66.05) * mm, "end": v(29.14, -66.03) * mm});
            skLineSegment(sketch, "E58", {"start": v(29.14, -66.03) * mm, "end": v(30.5, -66.4) * mm});
            skLineSegment(sketch, "E59", {"start": v(30.5, -66.4) * mm, "end": v(31.1, -66.8) * mm});
            skLineSegment(sketch, "E60", {"start": v(31.1, -66.8) * mm, "end": v(31.53, -67.3) * mm});
            skLineSegment(sketch, "E61", {"start": v(31.53, -67.3) * mm, "end": v(32.4, -68.45) * mm});
            skLineSegment(sketch, "E62", {"start": v(32.4, -68.45) * mm, "end": v(33.6, -67.88) * mm});
            skLineSegment(sketch, "E63", {"start": v(33.6, -67.88) * mm, "end": v(33.88, -67.68) * mm});
            skLineSegment(sketch, "E64", {"start": v(33.88, -67.68) * mm, "end": v(34.07, -67.34) * mm});
            skLineSegment(sketch, "E65", {"start": v(34.07, -67.34) * mm, "end": v(34.75, -61.87) * mm});
            skLineSegment(sketch, "E66", {"start": v(34.75, -61.87) * mm, "end": v(34.78, -60.13) * mm});
            skLineSegment(sketch, "E67", {"start": v(34.78, -60.13) * mm, "end": v(34.3, -59.3) * mm});
            skLineSegment(sketch, "E68", {"start": v(34.3, -59.3) * mm, "end": v(33.8, -59.15) * mm});
            skLineSegment(sketch, "E69", {"start": v(33.8, -59.15) * mm, "end": v(31.55, -59.25) * mm});
            skLineSegment(sketch, "E70", {"start": v(31.55, -59.25) * mm, "end": v(30.77, -59.2) * mm});
            skLineSegment(sketch, "E71", {"start": v(30.77, -59.2) * mm, "end": v(28.23, -58.7) * mm});
            skLineSegment(sketch, "E72", {"start": v(28.23, -58.7) * mm, "end": v(27.52, -58.68) * mm});
            skLineSegment(sketch, "E73", {"start": v(27.52, -58.68) * mm, "end": v(26.55, -59) * mm});
            skLineSegment(sketch, "E74", {"start": v(26.55, -59) * mm, "end": v(24.25, -59.78) * mm});
            skLineSegment(sketch, "E75", {"start": v(24.25, -59.78) * mm, "end": v(22.78, -60.17) * mm});
            skLineSegment(sketch, "E76", {"start": v(22.78, -60.17) * mm, "end": v(21.49, -60.36) * mm});
            skLineSegment(sketch, "E77", {"start": v(21.49, -60.36) * mm, "end": v(21.21, -60.3) * mm});
            skLineSegment(sketch, "E78", {"start": v(21.21, -60.3) * mm, "end": v(19.77, -59.81) * mm});
            skLineSegment(sketch, "E79", {"start": v(19.77, -59.81) * mm, "end": v(19.32, -59.73) * mm});
            skLineSegment(sketch, "E80", {"start": v(19.32, -59.73) * mm, "end": v(17.04, -59.65) * mm});
            skLineSegment(sketch, "E81", {"start": v(17.04, -59.65) * mm, "end": v(15.84, -59.38) * mm});
            skLineSegment(sketch, "E82", {"start": v(15.84, -59.38) * mm, "end": v(15.36, -58.76) * mm});
            skLineSegment(sketch, "E83", {"start": v(15.36, -58.76) * mm, "end": v(15.25, -58.06) * mm});
            skLineSegment(sketch, "E84", {"start": v(15.25, -58.06) * mm, "end": v(14.8, -58.12) * mm});
            skLineSegment(sketch, "E85", {"start": v(14.8, -58.12) * mm, "end": v(10.67, -58.68) * mm});
            skLineSegment(sketch, "E86", {"start": v(10.67, -58.68) * mm, "end": v(7.85, -58.84) * mm});
            skLineSegment(sketch, "E87", {"start": v(7.85, -58.84) * mm, "end": v(5, -58.33) * mm});
            skLineSegment(sketch, "E88", {"start": v(5, -58.33) * mm, "end": v(1.02, -57.07) * mm});
            skLineSegment(sketch, "E89", {"start": v(1.02, -57.07) * mm, "end": v(0, -56.55) * mm});
            skLineSegment(sketch, "E90", {"start": v(0, -56.55) * mm, "end": v(-6.33, -52.06) * mm});
            skLineSegment(sketch, "E91", {"start": v(-6.33, -52.06) * mm, "end": v(-7.15, -51.45) * mm});
            skLineSegment(sketch, "E92", {"start": v(-7.15, -51.45) * mm, "end": v(-10, -48.84) * mm});
            skLineSegment(sketch, "E93", {"start": v(-10, -48.84) * mm, "end": v(-12.96, -46.26) * mm});
            skLineSegment(sketch, "E94", {"start": v(-12.96, -46.26) * mm, "end": v(-14.28, -45.27) * mm});
            skLineSegment(sketch, "E95", {"start": v(-14.28, -45.27) * mm, "end": v(-20.33, -41.84) * mm});
            skLineSegment(sketch, "E96", {"start": v(-20.33, -41.84) * mm, "end": v(-27.37, -38.04) * mm});
            skLineSegment(sketch, "E97", {"start": v(-27.37, -38.04) * mm, "end": v(-28.3, -37.42) * mm});
            skLineSegment(sketch, "E98", {"start": v(-28.3, -37.42) * mm, "end": v(-31.34, -34.88) * mm});
            skLineSegment(sketch, "E99", {"start": v(-31.34, -34.88) * mm, "end": v(-32.4, -34.12) * mm});
            skLineSegment(sketch, "E100", {"start": v(-32.4, -34.12) * mm, "end": v(-35.63, -32.9) * mm});
            skLineSegment(sketch, "E101", {"start": v(-35.63, -32.9) * mm, "end": v(-36.37, -32.38) * mm});
            skLineSegment(sketch, "E102", {"start": v(-36.37, -32.38) * mm, "end": v(-36.58, -32.1) * mm});
            skLineSegment(sketch, "E103", {"start": v(-36.58, -32.1) * mm, "end": v(-36.76, -32) * mm});
            skLineSegment(sketch, "E104", {"start": v(-36.76, -32) * mm, "end": v(-38.16, -32.08) * mm});
            skLineSegment(sketch, "E105", {"start": v(-38.16, -32.08) * mm, "end": v(-38.3, -32.14) * mm});
            skLineSegment(sketch, "E106", {"start": v(-38.3, -32.14) * mm, "end": v(-38.3, -32.08) * mm});
            skLineSegment(sketch, "E107", {"start": v(-38.3, -32.08) * mm, "end": v(-37.98, -31.83) * mm});
            skLineSegment(sketch, "E108", {"start": v(-37.98, -31.83) * mm, "end": v(-37.87, -31.81) * mm});
            skLineSegment(sketch, "E109", {"start": v(-37.87, -31.81) * mm, "end": v(-36.9, -31.25) * mm});
            skLineSegment(sketch, "E110", {"start": v(-36.9, -31.25) * mm, "end": v(-35.15, -30.3) * mm});
            skLineSegment(sketch, "E111", {"start": v(-35.15, -30.3) * mm, "end": v(-30.89, -28.3) * mm});
            skLineSegment(sketch, "E112", {"start": v(-30.89, -28.3) * mm, "end": v(-28.17, -27.13) * mm});
            skLineSegment(sketch, "E113", {"start": v(-28.17, -27.13) * mm, "end": v(-23.7, -25.69) * mm});
            skLineSegment(sketch, "E114", {"start": v(-23.7, -25.69) * mm, "end": v(-22.85, -25.5) * mm});
            skLineSegment(sketch, "E115", {"start": v(-22.85, -25.5) * mm, "end": v(-17.31, -24.6) * mm});
            skLineSegment(sketch, "E116", {"start": v(-17.31, -24.6) * mm, "end": v(-14, -24.54) * mm});
            skLineSegment(sketch, "E117", {"start": v(-14, -24.54) * mm, "end": v(-13.34, -24.69) * mm});
            skLineSegment(sketch, "E118", {"start": v(-13.34, -24.69) * mm, "end": v(-6.63, -26.95) * mm});
            skLineSegment(sketch, "E119", {"start": v(-6.63, -26.95) * mm, "end": v(-5.52, -27.26) * mm});
            skLineSegment(sketch, "E120", {"start": v(-5.52, -27.26) * mm, "end": v(-1.7, -28.06) * mm});
            skLineSegment(sketch, "E121", {"start": v(-1.7, -28.06) * mm, "end": v(-0.44, -28.41) * mm});
            skLineSegment(sketch, "E122", {"start": v(-0.44, -28.41) * mm, "end": v(8.24, -31.37) * mm});
            skLineSegment(sketch, "E123", {"start": v(8.24, -31.37) * mm, "end": v(9.43, -32.02) * mm});
            skLineSegment(sketch, "E124", {"start": v(9.43, -32.02) * mm, "end": v(15.35, -36.65) * mm});
            skLineSegment(sketch, "E125", {"start": v(15.35, -36.65) * mm, "end": v(16.25, -36.89) * mm});
            skLineSegment(sketch, "E126", {"start": v(16.25, -36.89) * mm, "end": v(17.67, -36.67) * mm});
            skLineSegment(sketch, "E127", {"start": v(17.67, -36.67) * mm, "end": v(18.58, -36.3) * mm});
            skLineSegment(sketch, "E128", {"start": v(18.58, -36.3) * mm, "end": v(18.83, -36.11) * mm});
            skLineSegment(sketch, "E129", {"start": v(18.83, -36.11) * mm, "end": v(19.93, -35.29) * mm});
            skLineSegment(sketch, "E130", {"start": v(19.93, -35.29) * mm, "end": v(21.38, -33.7) * mm});
            skLineSegment(sketch, "E131", {"start": v(21.38, -33.7) * mm, "end": v(22.43, -32.86) * mm});
            skLineSegment(sketch, "E132", {"start": v(22.43, -32.86) * mm, "end": v(24.16, -31.93) * mm});
            skLineSegment(sketch, "E133", {"start": v(24.16, -31.93) * mm, "end": v(25.92, -30.86) * mm});
            skLineSegment(sketch, "E134", {"start": v(25.92, -30.86) * mm, "end": v(26.5, -30.31) * mm});
            skLineSegment(sketch, "E135", {"start": v(26.5, -30.31) * mm, "end": v(27.62, -28.7) * mm});
            skLineSegment(sketch, "E136", {"start": v(27.62, -28.7) * mm, "end": v(27.77, -28.36) * mm});
            skLineSegment(sketch, "E137", {"start": v(27.77, -28.36) * mm, "end": v(27.84, -28.03) * mm});
            skLineSegment(sketch, "E138", {"start": v(27.84, -28.03) * mm, "end": v(27.66, -24.92) * mm});
            skLineSegment(sketch, "E139", {"start": v(27.66, -24.92) * mm, "end": v(26.18, -14.74) * mm});
            skLineSegment(sketch, "E140", {"start": v(26.18, -14.74) * mm, "end": v(26.03, -11.04) * mm});
            skLineSegment(sketch, "E141", {"start": v(26.03, -11.04) * mm, "end": v(26.11, -7.96) * mm});
            skLineSegment(sketch, "E142", {"start": v(26.11, -7.96) * mm, "end": v(26.14, -6.74) * mm});
            skLineSegment(sketch, "E143", {"start": v(26.14, -6.74) * mm, "end": v(26.47, -4.87) * mm});
            skLineSegment(sketch, "E144", {"start": v(26.47, -4.87) * mm, "end": v(26.87, -2.4) * mm});
            skLineSegment(sketch, "E145", {"start": v(26.87, -2.4) * mm, "end": v(27.1, 0.64) * mm});
            skLineSegment(sketch, "E146", {"start": v(27.1, 0.64) * mm, "end": v(27.41, 2.86) * mm});
            skLineSegment(sketch, "E147", {"start": v(27.41, 2.86) * mm, "end": v(27.82, 4.78) * mm});
            skLineSegment(sketch, "E148", {"start": v(27.82, 4.78) * mm, "end": v(28.48, 7.73) * mm});
            skLineSegment(sketch, "E149", {"start": v(28.48, 7.73) * mm, "end": v(29.72, 12.56) * mm});
            skLineSegment(sketch, "E150", {"start": v(29.72, 12.56) * mm, "end": v(30.1, 13.5) * mm});
            skLineSegment(sketch, "E151", {"start": v(30.1, 13.5) * mm, "end": v(31.74, 16.02) * mm});
            skLineSegment(sketch, "E152", {"start": v(31.74, 16.02) * mm, "end": v(32.96, 17.46) * mm});
            skLineSegment(sketch, "E153", {"start": v(32.96, 17.46) * mm, "end": v(35.22, 19.65) * mm});
            skLineSegment(sketch, "E154", {"start": v(35.22, 19.65) * mm, "end": v(37.84, 22.4) * mm});
            skLineSegment(sketch, "E155", {"start": v(37.84, 22.4) * mm, "end": v(40.07, 24.43) * mm});
            skLineSegment(sketch, "E156", {"start": v(40.07, 24.43) * mm, "end": v(41.91, 25.66) * mm});
            skLineSegment(sketch, "E157", {"start": v(41.91, 25.66) * mm, "end": v(44.28, 27.05) * mm});
            skLineSegment(sketch, "E158", {"start": v(44.28, 27.05) * mm, "end": v(44.35, 26.95) * mm});
            skLineSegment(sketch, "E159", {"start": v(44.35, 26.95) * mm, "end": v(43.84, 25.75) * mm});
            skLineSegment(sketch, "E160", {"start": v(43.84, 25.75) * mm, "end": v(43.86, 25.55) * mm});
            skLineSegment(sketch, "E161", {"start": v(43.86, 25.55) * mm, "end": v(44.63, 24.7) * mm});
            skLineSegment(sketch, "E162", {"start": v(44.63, 24.7) * mm, "end": v(44.67, 24.62) * mm});
            skLineSegment(sketch, "E163", {"start": v(44.67, 24.62) * mm, "end": v(44.55, 24.56) * mm});
            skLineSegment(sketch, "E164", {"start": v(44.55, 24.56) * mm, "end": v(43.36, 23.8) * mm});
            skLineSegment(sketch, "E165", {"start": v(43.36, 23.8) * mm, "end": v(43.17, 23.64) * mm});
            skLineSegment(sketch, "E166", {"start": v(43.17, 23.64) * mm, "end": v(42.82, 22.75) * mm});
            skLineSegment(sketch, "E167", {"start": v(42.82, 22.75) * mm, "end": v(43.32, 18.82) * mm});
            skLineSegment(sketch, "E168", {"start": v(43.32, 18.82) * mm, "end": v(43.42, 18.24) * mm});
            skLineSegment(sketch, "E169", {"start": v(43.42, 18.24) * mm, "end": v(44.56, 13.67) * mm});
            skLineSegment(sketch, "E170", {"start": v(44.56, 13.67) * mm, "end": v(44.92, 11.78) * mm});
            skLineSegment(sketch, "E171", {"start": v(44.92, 11.78) * mm, "end": v(45.58, 6.9) * mm});
            skLineSegment(sketch, "E172", {"start": v(45.58, 6.9) * mm, "end": v(45.68, 6.31) * mm});
            skLineSegment(sketch, "E173", {"start": v(45.68, 6.31) * mm, "end": v(46.53, 3.77) * mm});
            skLineSegment(sketch, "E174", {"start": v(46.53, 3.77) * mm, "end": v(51.25, -9.7) * mm});
            skLineSegment(sketch, "E175", {"start": v(51.25, -9.7) * mm, "end": v(51.98, -12.1) * mm});
            skLineSegment(sketch, "E176", {"start": v(51.98, -12.1) * mm, "end": v(53.53, -16.55) * mm});
            skLineSegment(sketch, "E177", {"start": v(53.53, -16.55) * mm, "end": v(53.63, -17.53) * mm});
            skLineSegment(sketch, "E178", {"start": v(53.63, -17.53) * mm, "end": v(53.03, -22.14) * mm});
            skLineSegment(sketch, "E179", {"start": v(53.03, -22.14) * mm, "end": v(52.72, -23.08) * mm});
            skLineSegment(sketch, "E180", {"start": v(52.72, -23.08) * mm, "end": v(51.31, -25.57) * mm});
            skLineSegment(sketch, "E181", {"start": v(51.31, -25.57) * mm, "end": v(50.45, -27.54) * mm});
            skLineSegment(sketch, "E182", {"start": v(50.45, -27.54) * mm, "end": v(48.76, -32.6) * mm});
            skLineSegment(sketch, "E183", {"start": v(48.76, -32.6) * mm, "end": v(48.84, -33.37) * mm});
            skLineSegment(sketch, "E184", {"start": v(48.84, -33.37) * mm, "end": v(49.05, -33.75) * mm});
            skLineSegment(sketch, "E185", {"start": v(49.05, -33.75) * mm, "end": v(49, -35.32) * mm});
            skLineSegment(sketch, "E186", {"start": v(49, -35.32) * mm, "end": v(48.78, -35.95) * mm});
            skLineSegment(sketch, "E187", {"start": v(48.78, -35.95) * mm, "end": v(48.86, -36.72) * mm});
            skLineSegment(sketch, "E188", {"start": v(48.86, -36.72) * mm, "end": v(48.82, -37.24) * mm});
            skLineSegment(sketch, "E189", {"start": v(48.82, -37.24) * mm, "end": v(47.99, -39.92) * mm});
            skLineSegment(sketch, "E190", {"start": v(47.99, -39.92) * mm, "end": v(47.78, -40.33) * mm});
            skLineSegment(sketch, "E191", {"start": v(47.78, -40.33) * mm, "end": v(46.9, -41.6) * mm});
            skLineSegment(sketch, "E192", {"start": v(46.9, -41.6) * mm, "end": v(45.67, -43.99) * mm});
            skLineSegment(sketch, "E193", {"start": v(45.67, -43.99) * mm, "end": v(45.55, -44.62) * mm});
            skLineSegment(sketch, "E194", {"start": v(45.55, -44.62) * mm, "end": v(45.6, -46.43) * mm});
            skLineSegment(sketch, "E195", {"start": v(45.6, -46.43) * mm, "end": v(45.95, -47.5) * mm});
            skLineSegment(sketch, "E196", {"start": v(45.95, -47.5) * mm, "end": v(45.98, -47.54) * mm});
            skLineSegment(sketch, "E197", {"start": v(45.98, -47.54) * mm, "end": v(46.42, -47.92) * mm});
            skLineSegment(sketch, "E198", {"start": v(46.42, -47.92) * mm, "end": v(48.1, -48.8) * mm});
            skLineSegment(sketch, "E199", {"start": v(48.1, -48.8) * mm, "end": v(50.93, -50.32) * mm});
            skLineSegment(sketch, "E200", {"start": v(50.93, -50.32) * mm, "end": v(54.74, -51.78) * mm});
            skLineSegment(sketch, "E201", {"start": v(54.74, -51.78) * mm, "end": v(55.04, -51.7) * mm});
            skLineSegment(sketch, "E202", {"start": v(55.04, -51.7) * mm, "end": v(56.68, -50.3) * mm});
            skLineSegment(sketch, "E203", {"start": v(56.68, -50.3) * mm, "end": v(56.86, -50.11) * mm});
            skLineSegment(sketch, "E204", {"start": v(56.86, -50.11) * mm, "end": v(56.54, -49.9) * mm});
            skLineSegment(sketch, "E205", {"start": v(56.54, -49.9) * mm, "end": v(56.1, -49.36) * mm});
            skLineSegment(sketch, "E206", {"start": v(56.1, -49.36) * mm, "end": v(55.8, -48.7) * mm});
            skLineSegment(sketch, "E207", {"start": v(55.8, -48.7) * mm, "end": v(55.75, -47.82) * mm});
            skLineSegment(sketch, "E208", {"start": v(55.75, -47.82) * mm, "end": v(56.06, -47.47) * mm});
            skLineSegment(sketch, "E209", {"start": v(56.06, -47.47) * mm, "end": v(56.58, -46.66) * mm});
            skLineSegment(sketch, "E210", {"start": v(56.58, -46.66) * mm, "end": v(56.56, -46.47) * mm});
            skLineSegment(sketch, "E211", {"start": v(56.56, -46.47) * mm, "end": v(56.48, -45.22) * mm});
            skLineSegment(sketch, "E212", {"start": v(56.48, -45.22) * mm, "end": v(56.52, -44.92) * mm});
            skLineSegment(sketch, "E213", {"start": v(56.52, -44.92) * mm, "end": v(56.86, -44.22) * mm});
            skLineSegment(sketch, "E214", {"start": v(56.86, -44.22) * mm, "end": v(57.23, -43.93) * mm});
            skLineSegment(sketch, "E215", {"start": v(57.23, -43.93) * mm, "end": v(58.31, -43.62) * mm});
            skLineSegment(sketch, "E216", {"start": v(58.31, -43.62) * mm, "end": v(58.74, -43.49) * mm});
            skLineSegment(sketch, "E217", {"start": v(58.74, -43.49) * mm, "end": v(58.77, -43.24) * mm});
            skLineSegment(sketch, "E218", {"start": v(58.77, -43.24) * mm, "end": v(58.84, -42.6) * mm});
            skLineSegment(sketch, "E219", {"start": v(58.84, -42.6) * mm, "end": v(59.33, -42.13) * mm});
            skLineSegment(sketch, "E220", {"start": v(59.33, -42.13) * mm, "end": v(59.46, -42) * mm});
            skLineSegment(sketch, "E221", {"start": v(59.46, -42) * mm, "end": v(60.16, -41.75) * mm});
            skLineSegment(sketch, "E222", {"start": v(60.16, -41.75) * mm, "end": v(60.63, -41.75) * mm});
            skLineSegment(sketch, "E223", {"start": v(60.63, -41.75) * mm, "end": v(61.17, -41.86) * mm});
            skLineSegment(sketch, "E224", {"start": v(61.17, -41.86) * mm, "end": v(62.12, -42.25) * mm});
            skLineSegment(sketch, "E225", {"start": v(62.12, -42.25) * mm, "end": v(62.35, -41.78) * mm});
            skLineSegment(sketch, "E226", {"start": v(62.35, -41.78) * mm, "end": v(63.07, -41.74) * mm});
            skLineSegment(sketch, "E227", {"start": v(63.07, -41.74) * mm, "end": v(63.31, -41.78) * mm});
            skLineSegment(sketch, "E228", {"start": v(63.31, -41.78) * mm, "end": v(64.5, -42.44) * mm});
            skLineSegment(sketch, "E229", {"start": v(64.5, -42.44) * mm, "end": v(65.67, -43.22) * mm});
            skLineSegment(sketch, "E230", {"start": v(65.67, -43.22) * mm, "end": v(66.06, -43.5) * mm});
            skLineSegment(sketch, "E231", {"start": v(66.06, -43.5) * mm, "end": v(65.91, -43.69) * mm});
            skLineSegment(sketch, "E232", {"start": v(65.91, -43.69) * mm, "end": v(62.8, -47.05) * mm});
            skLineSegment(sketch, "E233", {"start": v(62.8, -47.05) * mm, "end": v(58.53, -51.7) * mm});
            skLineSegment(sketch, "E234", {"start": v(58.53, -51.7) * mm, "end": v(57.44, -52.86) * mm});
            skLineSegment(sketch, "E235", {"start": v(57.44, -52.86) * mm, "end": v(53.42, -56.12) * mm});
            skLineSegment(sketch, "E236", {"start": v(53.42, -56.12) * mm, "end": v(48.64, -59.98) * mm});
            skLineSegment(sketch, "E237", {"start": v(48.64, -59.98) * mm, "end": v(47.58, -60.9) * mm});
            skLineSegment(sketch, "E238", {"start": v(20.8, -47.53) * mm, "end": v(21.29, -46.28) * mm});
            skLineSegment(sketch, "E239", {"start": v(21.29, -46.28) * mm, "end": v(22.54, -43.54) * mm});
            skLineSegment(sketch, "E240", {"start": v(22.54, -43.54) * mm, "end": v(23.82, -42.25) * mm});
            skLineSegment(sketch, "E241", {"start": v(23.82, -42.25) * mm, "end": v(25.86, -41.05) * mm});
            skLineSegment(sketch, "E242", {"start": v(25.86, -41.05) * mm, "end": v(27.03, -40.8) * mm});
            skLineSegment(sketch, "E243", {"start": v(27.03, -40.8) * mm, "end": v(28.48, -40.93) * mm});
            skLineSegment(sketch, "E244", {"start": v(28.48, -40.93) * mm, "end": v(28.55, -40.84) * mm});
            skLineSegment(sketch, "E245", {"start": v(28.55, -40.84) * mm, "end": v(29.39, -38.96) * mm});
            skLineSegment(sketch, "E246", {"start": v(29.39, -38.96) * mm, "end": v(30.1, -37.88) * mm});
            skLineSegment(sketch, "E247", {"start": v(30.1, -37.88) * mm, "end": v(31.07, -37.08) * mm});
            skLineSegment(sketch, "E248", {"start": v(31.07, -37.08) * mm, "end": v(31.87, -36.55) * mm});
            skLineSegment(sketch, "E249", {"start": v(31.87, -36.55) * mm, "end": v(33.03, -35.94) * mm});
            skLineSegment(sketch, "E250", {"start": v(33.03, -35.94) * mm, "end": v(34.9, -35.18) * mm});
            skLineSegment(sketch, "E251", {"start": v(34.9, -35.18) * mm, "end": v(36.35, -34.85) * mm});
            skLineSegment(sketch, "E252", {"start": v(36.35, -34.85) * mm, "end": v(37.37, -34.89) * mm});
            skLineSegment(sketch, "E253", {"start": v(37.37, -34.89) * mm, "end": v(39, -35.4) * mm});
            skLineSegment(sketch, "E254", {"start": v(39, -35.4) * mm, "end": v(39.9, -35.82) * mm});
            skLineSegment(sketch, "E255", {"start": v(39.9, -35.82) * mm, "end": v(41.1, -36.56) * mm});
            skLineSegment(sketch, "E256", {"start": v(41.1, -36.56) * mm, "end": v(41.47, -36.77) * mm});
            skLineSegment(sketch, "E257", {"start": v(41.47, -36.77) * mm, "end": v(41.36, -36.12) * mm});
            skLineSegment(sketch, "E258", {"start": v(41.36, -36.12) * mm, "end": v(40.36, -31.72) * mm});
            skLineSegment(sketch, "E259", {"start": v(40.36, -31.72) * mm, "end": v(39.7, -30.92) * mm});
            skLineSegment(sketch, "E260", {"start": v(39.7, -30.92) * mm, "end": v(36.2, -29.42) * mm});
            skLineSegment(sketch, "E261", {"start": v(36.2, -29.42) * mm, "end": v(35.72, -29.2) * mm});
            skLineSegment(sketch, "E262", {"start": v(35.72, -29.2) * mm, "end": v(37.5, -28.5) * mm});
            skLineSegment(sketch, "E263", {"start": v(37.5, -28.5) * mm, "end": v(39.06, -28.3) * mm});
            skLineSegment(sketch, "E264", {"start": v(39.06, -28.3) * mm, "end": v(39.09, -27.95) * mm});
            skLineSegment(sketch, "E265", {"start": v(39.09, -27.95) * mm, "end": v(39.23, -26.17) * mm});
            skLineSegment(sketch, "E266", {"start": v(39.23, -26.17) * mm, "end": v(39.6, -25.14) * mm});
            skLineSegment(sketch, "E267", {"start": v(39.6, -25.14) * mm, "end": v(40.62, -23.68) * mm});
            skLineSegment(sketch, "E268", {"start": v(40.62, -23.68) * mm, "end": v(41.06, -22.56) * mm});
            skLineSegment(sketch, "E269", {"start": v(41.06, -22.56) * mm, "end": v(41.66, -18.74) * mm});
            skLineSegment(sketch, "E270", {"start": v(41.66, -18.74) * mm, "end": v(41.57, -17.54) * mm});
            skLineSegment(sketch, "E271", {"start": v(41.57, -17.54) * mm, "end": v(38.3, -7.6) * mm});
            skLineSegment(sketch, "E272", {"start": v(38.3, -7.6) * mm, "end": v(37.4, -5.07) * mm});
            skLineSegment(sketch, "E273", {"start": v(37.4, -5.07) * mm, "end": v(36.18, -2.4) * mm});
            skLineSegment(sketch, "E274", {"start": v(36.18, -2.4) * mm, "end": v(35.89, -1.2) * mm});
            skLineSegment(sketch, "E275", {"start": v(35.89, -1.2) * mm, "end": v(35.06, 7.41) * mm});
            skLineSegment(sketch, "E276", {"start": v(35.06, 7.41) * mm, "end": v(35.01, 8.25) * mm});
            skLineSegment(sketch, "E277", {"start": v(35.01, 8.25) * mm, "end": v(35.11, 10.78) * mm});
            skLineSegment(sketch, "E278", {"start": v(35.11, 10.78) * mm, "end": v(35.22, 11.52) * mm});
            skLineSegment(sketch, "E279", {"start": v(35.22, 11.52) * mm, "end": v(36.13, 15.37) * mm});
            skLineSegment(sketch, "E280", {"start": v(36.13, 15.37) * mm, "end": v(36.72, 16.84) * mm});
            skLineSegment(sketch, "E281", {"start": v(36.72, 16.84) * mm, "end": v(38.93, 20.63) * mm});
            skLineSegment(sketch, "E282", {"start": v(38.93, 20.63) * mm, "end": v(39.09, 20.95) * mm});
            skLineSegment(sketch, "E283", {"start": v(39.09, 20.95) * mm, "end": v(39.03, 21) * mm});
            skLineSegment(sketch, "E284", {"start": v(39.03, 21) * mm, "end": v(38.6, 20.6) * mm});
            skLineSegment(sketch, "E285", {"start": v(38.6, 20.6) * mm, "end": v(36.6, 18.68) * mm});
            skLineSegment(sketch, "E286", {"start": v(36.6, 18.68) * mm, "end": v(32.94, 14.81) * mm});
            skLineSegment(sketch, "E287", {"start": v(32.94, 14.81) * mm, "end": v(32.43, 13.84) * mm});
            skLineSegment(sketch, "E288", {"start": v(32.43, 13.84) * mm, "end": v(29.98, 2.98) * mm});
            skLineSegment(sketch, "E289", {"start": v(29.98, 2.98) * mm, "end": v(29.8, 1.96) * mm});
            skLineSegment(sketch, "E290", {"start": v(29.8, 1.96) * mm, "end": v(28.73, -11.78) * mm});
            skLineSegment(sketch, "E291", {"start": v(28.73, -11.78) * mm, "end": v(28.74, -12.47) * mm});
            skLineSegment(sketch, "E292", {"start": v(28.74, -12.47) * mm, "end": v(29.85, -19.33) * mm});
            skLineSegment(sketch, "E293", {"start": v(29.85, -19.33) * mm, "end": v(31.03, -24.81) * mm});
            skLineSegment(sketch, "E294", {"start": v(31.03, -24.81) * mm, "end": v(31.19, -25.95) * mm});
            skLineSegment(sketch, "E295", {"start": v(31.19, -25.95) * mm, "end": v(31.25, -27.82) * mm});
            skLineSegment(sketch, "E296", {"start": v(31.25, -27.82) * mm, "end": v(31.38, -28.68) * mm});
            skLineSegment(sketch, "E297", {"start": v(31.38, -28.68) * mm, "end": v(32.52, -30.9) * mm});
            skLineSegment(sketch, "E298", {"start": v(32.52, -30.9) * mm, "end": v(33.4, -31.37) * mm});
            skLineSegment(sketch, "E299", {"start": v(33.4, -31.37) * mm, "end": v(33.93, -31.42) * mm});
            skLineSegment(sketch, "E300", {"start": v(33.93, -31.42) * mm, "end": v(34.68, -31.69) * mm});
            skLineSegment(sketch, "E301", {"start": v(34.68, -31.69) * mm, "end": v(34.78, -32.68) * mm});
            skLineSegment(sketch, "E302", {"start": v(34.78, -32.68) * mm, "end": v(33.89, -32.7) * mm});
            skLineSegment(sketch, "E303", {"start": v(33.89, -32.7) * mm, "end": v(31.46, -32.57) * mm});
            skLineSegment(sketch, "E304", {"start": v(31.46, -32.57) * mm, "end": v(31.12, -32.58) * mm});
            skLineSegment(sketch, "E305", {"start": v(31.12, -32.58) * mm, "end": v(28.52, -33.18) * mm});
            skLineSegment(sketch, "E306", {"start": v(28.52, -33.18) * mm, "end": v(26.84, -33.83) * mm});
            skLineSegment(sketch, "E307", {"start": v(26.84, -33.83) * mm, "end": v(24.22, -35.22) * mm});
            skLineSegment(sketch, "E308", {"start": v(24.22, -35.22) * mm, "end": v(23.82, -35.5) * mm});
            skLineSegment(sketch, "E309", {"start": v(23.82, -35.5) * mm, "end": v(22.94, -36.42) * mm});
            skLineSegment(sketch, "E310", {"start": v(22.94, -36.42) * mm, "end": v(21.73, -37.88) * mm});
            skLineSegment(sketch, "E311", {"start": v(21.73, -37.88) * mm, "end": v(20.41, -39.96) * mm});
            skLineSegment(sketch, "E312", {"start": v(20.41, -39.96) * mm, "end": v(20.03, -40.74) * mm});
            skLineSegment(sketch, "E313", {"start": v(20.03, -40.74) * mm, "end": v(19.31, -42.64) * mm});
            skLineSegment(sketch, "E314", {"start": v(19.31, -42.64) * mm, "end": v(19.17, -43.62) * mm});
            skLineSegment(sketch, "E315", {"start": v(19.17, -43.62) * mm, "end": v(19.37, -46.82) * mm});
            skLineSegment(sketch, "E316", {"start": v(19.37, -46.82) * mm, "end": v(19.4, -47.2) * mm});
            skLineSegment(sketch, "E317", {"start": v(19.4, -47.2) * mm, "end": v(20.8, -47.53) * mm});
            skLineSegment(sketch, "E318", {"start": v(-32.68, -30.89) * mm, "end": v(-32.66, -30.96) * mm});
            skLineSegment(sketch, "E319", {"start": v(-32.66, -30.96) * mm, "end": v(-32.33, -30.94) * mm});
            skLineSegment(sketch, "E320", {"start": v(-32.33, -30.94) * mm, "end": v(-26.39, -30.54) * mm});
            skLineSegment(sketch, "E321", {"start": v(-26.39, -30.54) * mm, "end": v(-25.15, -30.65) * mm});
            skLineSegment(sketch, "E322", {"start": v(-25.15, -30.65) * mm, "end": v(-23.63, -31.01) * mm});
            skLineSegment(sketch, "E323", {"start": v(-23.63, -31.01) * mm, "end": v(-23.23, -31.07) * mm});
            skLineSegment(sketch, "E324", {"start": v(-23.23, -31.07) * mm, "end": v(-21.85, -30.89) * mm});
            skLineSegment(sketch, "E325", {"start": v(-21.85, -30.89) * mm, "end": v(-21.54, -30.85) * mm});
            skLineSegment(sketch, "E326", {"start": v(-21.54, -30.85) * mm, "end": v(-19.91, -31.31) * mm});
            skLineSegment(sketch, "E327", {"start": v(-19.91, -31.31) * mm, "end": v(-19.14, -31.48) * mm});
            skLineSegment(sketch, "E328", {"start": v(-19.14, -31.48) * mm, "end": v(-17.33, -31.66) * mm});
            skLineSegment(sketch, "E329", {"start": v(-17.33, -31.66) * mm, "end": v(-16.1, -32) * mm});
            skLineSegment(sketch, "E330", {"start": v(-16.1, -32) * mm, "end": v(-15.12, -32.4) * mm});
            skLineSegment(sketch, "E331", {"start": v(-15.12, -32.4) * mm, "end": v(-13.74, -33.25) * mm});
            skLineSegment(sketch, "E332", {"start": v(-13.74, -33.25) * mm, "end": v(-12.88, -33.81) * mm});
            skLineSegment(sketch, "E333", {"start": v(-12.88, -33.81) * mm, "end": v(-9.17, -36.54) * mm});
            skLineSegment(sketch, "E334", {"start": v(-9.17, -36.54) * mm, "end": v(-8.82, -36.8) * mm});
            skLineSegment(sketch, "E335", {"start": v(-8.82, -36.8) * mm, "end": v(-5.15, -39.6) * mm});
            skLineSegment(sketch, "E336", {"start": v(-5.15, -39.6) * mm, "end": v(-3.36, -41) * mm});
            skLineSegment(sketch, "E337", {"start": v(-3.36, -41) * mm, "end": v(-1.93, -42.25) * mm});
            skLineSegment(sketch, "E338", {"start": v(-1.93, -42.25) * mm, "end": v(-0.88, -43.22) * mm});
            skLineSegment(sketch, "E339", {"start": v(-0.88, -43.22) * mm, "end": v(1.1, -45.25) * mm});
            skLineSegment(sketch, "E340", {"start": v(1.1, -45.25) * mm, "end": v(2, -45.8) * mm});
            skLineSegment(sketch, "E341", {"start": v(2, -45.8) * mm, "end": v(5.46, -46.67) * mm});
            skLineSegment(sketch, "E342", {"start": v(5.46, -46.67) * mm, "end": v(6.42, -46.8) * mm});
            skLineSegment(sketch, "E343", {"start": v(6.42, -46.8) * mm, "end": v(8.53, -46.75) * mm});
            skLineSegment(sketch, "E344", {"start": v(8.53, -46.75) * mm, "end": v(10.77, -46.59) * mm});
            skLineSegment(sketch, "E345", {"start": v(10.77, -46.59) * mm, "end": v(11.32, -46.34) * mm});
            skLineSegment(sketch, "E346", {"start": v(11.32, -46.34) * mm, "end": v(12.03, -45.56) * mm});
            skLineSegment(sketch, "E347", {"start": v(12.03, -45.56) * mm, "end": v(12.67, -44.9) * mm});
            skLineSegment(sketch, "E348", {"start": v(12.67, -44.9) * mm, "end": v(13, -45.48) * mm});
            skLineSegment(sketch, "E349", {"start": v(13, -45.48) * mm, "end": v(13.07, -46.45) * mm});
            skLineSegment(sketch, "E350", {"start": v(13.07, -46.45) * mm, "end": v(13.35, -47.33) * mm});
            skLineSegment(sketch, "E351", {"start": v(13.35, -47.33) * mm, "end": v(13.92, -47.38) * mm});
            skLineSegment(sketch, "E352", {"start": v(13.92, -47.38) * mm, "end": v(14.67, -46.12) * mm});
            skLineSegment(sketch, "E353", {"start": v(14.67, -46.12) * mm, "end": v(14.75, -45.85) * mm});
            skLineSegment(sketch, "E354", {"start": v(14.75, -45.85) * mm, "end": v(15.4, -42.29) * mm});
            skLineSegment(sketch, "E355", {"start": v(15.4, -42.29) * mm, "end": v(15.39, -42.02) * mm});
            skLineSegment(sketch, "E356", {"start": v(15.39, -42.02) * mm, "end": v(14.73, -40.81) * mm});
            skLineSegment(sketch, "E357", {"start": v(14.73, -40.81) * mm, "end": v(14.63, -40.7) * mm});
            skLineSegment(sketch, "E358", {"start": v(14.63, -40.7) * mm, "end": v(13.8, -39.34) * mm});
            skLineSegment(sketch, "E359", {"start": v(13.8, -39.34) * mm, "end": v(13.09, -38.53) * mm});
            skLineSegment(sketch, "E360", {"start": v(13.09, -38.53) * mm, "end": v(9.21, -35.5) * mm});
            skLineSegment(sketch, "E361", {"start": v(9.21, -35.5) * mm, "end": v(8.12, -34.87) * mm});
            skLineSegment(sketch, "E362", {"start": v(8.12, -34.87) * mm, "end": v(6.22, -34.18) * mm});
            skLineSegment(sketch, "E363", {"start": v(6.22, -34.18) * mm, "end": v(1.51, -32.18) * mm});
            skLineSegment(sketch, "E364", {"start": v(1.51, -32.18) * mm, "end": v(1.14, -32.02) * mm});
            skLineSegment(sketch, "E365", {"start": v(1.14, -32.02) * mm, "end": v(-4.92, -29.7) * mm});
            skLineSegment(sketch, "E366", {"start": v(-4.92, -29.7) * mm, "end": v(-5.9, -29.43) * mm});
            skLineSegment(sketch, "E367", {"start": v(-5.9, -29.43) * mm, "end": v(-9.36, -28.74) * mm});
            skLineSegment(sketch, "E368", {"start": v(-9.36, -28.74) * mm, "end": v(-10.49, -28.39) * mm});
            skLineSegment(sketch, "E369", {"start": v(-10.49, -28.39) * mm, "end": v(-13.64, -27.03) * mm});
            skLineSegment(sketch, "E370", {"start": v(-13.64, -27.03) * mm, "end": v(-14.82, -26.78) * mm});
            skLineSegment(sketch, "E371", {"start": v(-14.82, -26.78) * mm, "end": v(-16.97, -26.73) * mm});
            skLineSegment(sketch, "E372", {"start": v(-16.97, -26.73) * mm, "end": v(-18.14, -26.85) * mm});
            skLineSegment(sketch, "E373", {"start": v(-18.14, -26.85) * mm, "end": v(-20.83, -27.5) * mm});
            skLineSegment(sketch, "E374", {"start": v(-20.83, -27.5) * mm, "end": v(-24.25, -28.33) * mm});
            skLineSegment(sketch, "E375", {"start": v(-24.25, -28.33) * mm, "end": v(-32.15, -30.7) * mm});
            skLineSegment(sketch, "E376", {"start": v(-32.15, -30.7) * mm, "end": v(-32.68, -30.89) * mm});
            skLineSegment(sketch, "E377", {"start": v(47.09, -11.27) * mm, "end": v(47.19, -11.73) * mm});
            skLineSegment(sketch, "E378", {"start": v(47.19, -11.73) * mm, "end": v(48.59, -18.98) * mm});
            skLineSegment(sketch, "E379", {"start": v(48.59, -18.98) * mm, "end": v(48.56, -19.94) * mm});
            skLineSegment(sketch, "E380", {"start": v(48.56, -19.94) * mm, "end": v(47.52, -24.05) * mm});
            skLineSegment(sketch, "E381", {"start": v(47.52, -24.05) * mm, "end": v(47.04, -25.02) * mm});
            skLineSegment(sketch, "E382", {"start": v(47.04, -25.02) * mm, "end": v(46.28, -26) * mm});
            skLineSegment(sketch, "E383", {"start": v(46.28, -26) * mm, "end": v(46, -26.62) * mm});
            skLineSegment(sketch, "E384", {"start": v(46, -26.62) * mm, "end": v(45.8, -28.48) * mm});
            skLineSegment(sketch, "E385", {"start": v(45.8, -28.48) * mm, "end": v(45.94, -29.16) * mm});
            skLineSegment(sketch, "E386", {"start": v(45.94, -29.16) * mm, "end": v(46.74, -30.14) * mm});
            skLineSegment(sketch, "E387", {"start": v(46.74, -30.14) * mm, "end": v(47.27, -29.43) * mm});
            skLineSegment(sketch, "E388", {"start": v(47.27, -29.43) * mm, "end": v(48.05, -27.16) * mm});
            skLineSegment(sketch, "E389", {"start": v(48.05, -27.16) * mm, "end": v(49, -25.27) * mm});
            skLineSegment(sketch, "E390", {"start": v(49, -25.27) * mm, "end": v(49.54, -24.15) * mm});
            skLineSegment(sketch, "E391", {"start": v(49.54, -24.15) * mm, "end": v(50.34, -22.05) * mm});
            skLineSegment(sketch, "E392", {"start": v(50.34, -22.05) * mm, "end": v(50.45, -21.63) * mm});
            skLineSegment(sketch, "E393", {"start": v(50.45, -21.63) * mm, "end": v(51, -18.25) * mm});
            skLineSegment(sketch, "E394", {"start": v(51, -18.25) * mm, "end": v(50.9, -16.77) * mm});
            skLineSegment(sketch, "E395", {"start": v(50.9, -16.77) * mm, "end": v(49.21, -10.9) * mm});
            skLineSegment(sketch, "E396", {"start": v(49.21, -10.9) * mm, "end": v(48, -7) * mm});
            skLineSegment(sketch, "E397", {"start": v(48, -7) * mm, "end": v(44.76, 2) * mm});
            skLineSegment(sketch, "E398", {"start": v(44.76, 2) * mm, "end": v(44.48, 2.95) * mm});
            skLineSegment(sketch, "E399", {"start": v(44.48, 2.95) * mm, "end": v(41.35, 17.7) * mm});
            skLineSegment(sketch, "E400", {"start": v(41.35, 17.7) * mm, "end": v(41.23, 18.47) * mm});
            skLineSegment(sketch, "E401", {"start": v(41.23, 18.47) * mm, "end": v(41.03, 20.33) * mm});
            skLineSegment(sketch, "E402", {"start": v(41.03, 20.33) * mm, "end": v(40.88, 20.78) * mm});
            skLineSegment(sketch, "E403", {"start": v(40.88, 20.78) * mm, "end": v(40.82, 20.55) * mm});
            skLineSegment(sketch, "E404", {"start": v(40.82, 20.55) * mm, "end": v(40.78, 17.63) * mm});
            skLineSegment(sketch, "E405", {"start": v(40.78, 17.63) * mm, "end": v(40.83, 16.11) * mm});
            skLineSegment(sketch, "E406", {"start": v(40.83, 16.11) * mm, "end": v(40.8, 15.36) * mm});
            skLineSegment(sketch, "E407", {"start": v(40.8, 15.36) * mm, "end": v(40.9, 13.6) * mm});
            skLineSegment(sketch, "E408", {"start": v(40.9, 13.6) * mm, "end": v(41.03, 12.45) * mm});
            skLineSegment(sketch, "E409", {"start": v(41.03, 12.45) * mm, "end": v(40.88, 8.84) * mm});
            skLineSegment(sketch, "E410", {"start": v(40.88, 8.84) * mm, "end": v(40.37, 7.67) * mm});
            skLineSegment(sketch, "E411", {"start": v(40.37, 7.67) * mm, "end": v(39.64, 6.94) * mm});
            skLineSegment(sketch, "E412", {"start": v(39.64, 6.94) * mm, "end": v(39.3, 6.58) * mm});
            skLineSegment(sketch, "E413", {"start": v(39.3, 6.58) * mm, "end": v(39.87, 6.44) * mm});
            skLineSegment(sketch, "E414", {"start": v(39.87, 6.44) * mm, "end": v(40.63, 6.41) * mm});
            skLineSegment(sketch, "E415", {"start": v(40.63, 6.41) * mm, "end": v(41.65, 6.62) * mm});
            skLineSegment(sketch, "E416", {"start": v(41.65, 6.62) * mm, "end": v(41.72, 6.37) * mm});
            skLineSegment(sketch, "E417", {"start": v(41.72, 6.37) * mm, "end": v(42.42, 4.14) * mm});
            skLineSegment(sketch, "E418", {"start": v(42.42, 4.14) * mm, "end": v(43.04, 1.45) * mm});
            skLineSegment(sketch, "E419", {"start": v(43.04, 1.45) * mm, "end": v(43.31, -0.11) * mm});
            skLineSegment(sketch, "E420", {"start": v(43.31, -0.11) * mm, "end": v(44.17, -3.04) * mm});
            skLineSegment(sketch, "E421", {"start": v(44.17, -3.04) * mm, "end": v(44.57, -3.99) * mm});
            skLineSegment(sketch, "E422", {"start": v(44.57, -3.99) * mm, "end": v(46, -7.16) * mm});
            skLineSegment(sketch, "E423", {"start": v(46, -7.16) * mm, "end": v(46.23, -7.84) * mm});
            skLineSegment(sketch, "E424", {"start": v(46.23, -7.84) * mm, "end": v(46.58, -9.63) * mm});
            skLineSegment(sketch, "E425", {"start": v(46.58, -9.63) * mm, "end": v(46.33, -10.36) * mm});
            skLineSegment(sketch, "E426", {"start": v(46.33, -10.36) * mm, "end": v(45.55, -11.33) * mm});
            skLineSegment(sketch, "E427", {"start": v(45.55, -11.33) * mm, "end": v(47.09, -11.27) * mm});
            skLineSegment(sketch, "E428", {"start": v(12.7, -55.92) * mm, "end": v(12.53, -55.73) * mm});
            skLineSegment(sketch, "E429", {"start": v(12.53, -55.73) * mm, "end": v(11.15, -54.43) * mm});
            skLineSegment(sketch, "E430", {"start": v(11.15, -54.43) * mm, "end": v(10.41, -54.05) * mm});
            skLineSegment(sketch, "E431", {"start": v(10.41, -54.05) * mm, "end": v(7.55, -53.63) * mm});
            skLineSegment(sketch, "E432", {"start": v(7.55, -53.63) * mm, "end": v(6.55, -53.56) * mm});
            skLineSegment(sketch, "E433", {"start": v(6.55, -53.56) * mm, "end": v(6.16, -53.5) * mm});
            skLineSegment(sketch, "E434", {"start": v(6.16, -53.5) * mm, "end": v(2.88, -52.3) * mm});
            skLineSegment(sketch, "E435", {"start": v(2.88, -52.3) * mm, "end": v(2.04, -51.9) * mm});
            skLineSegment(sketch, "E436", {"start": v(2.04, -51.9) * mm, "end": v(0.97, -51.34) * mm});
            skLineSegment(sketch, "E437", {"start": v(0.97, -51.34) * mm, "end": v(-2.4, -49.27) * mm});
            skLineSegment(sketch, "E438", {"start": v(-2.4, -49.27) * mm, "end": v(-2.88, -48.64) * mm});
            skLineSegment(sketch, "E439", {"start": v(-2.88, -48.64) * mm, "end": v(-3.08, -45.88) * mm});
            skLineSegment(sketch, "E440", {"start": v(-3.08, -45.88) * mm, "end": v(-3.1, -45.58) * mm});
            skLineSegment(sketch, "E441", {"start": v(-3.1, -45.58) * mm, "end": v(-4.52, -47.62) * mm});
            skLineSegment(sketch, "E442", {"start": v(-4.52, -47.62) * mm, "end": v(-4.7, -47.55) * mm});
            skLineSegment(sketch, "E443", {"start": v(-4.7, -47.55) * mm, "end": v(-6.01, -46.66) * mm});
            skLineSegment(sketch, "E444", {"start": v(-6.01, -46.66) * mm, "end": v(-8.22, -44.88) * mm});
            skLineSegment(sketch, "E445", {"start": v(-8.22, -44.88) * mm, "end": v(-10.08, -43.47) * mm});
            skLineSegment(sketch, "E446", {"start": v(-10.08, -43.47) * mm, "end": v(-13.65, -41.24) * mm});
            skLineSegment(sketch, "E447", {"start": v(-13.65, -41.24) * mm, "end": v(-15.96, -39.77) * mm});
            skLineSegment(sketch, "E448", {"start": v(-15.96, -39.77) * mm, "end": v(-21.24, -35.86) * mm});
            skLineSegment(sketch, "E449", {"start": v(-21.24, -35.86) * mm, "end": v(-22.3, -35.4) * mm});
            skLineSegment(sketch, "E450", {"start": v(-22.3, -35.4) * mm, "end": v(-25, -34.94) * mm});
            skLineSegment(sketch, "E451", {"start": v(-25, -34.94) * mm, "end": v(-26.12, -34.58) * mm});
            skLineSegment(sketch, "E452", {"start": v(-26.12, -34.58) * mm, "end": v(-29.6, -32.92) * mm});
            skLineSegment(sketch, "E453", {"start": v(-29.6, -32.92) * mm, "end": v(-30.17, -32.79) * mm});
            skLineSegment(sketch, "E454", {"start": v(-30.17, -32.79) * mm, "end": v(-28.67, -33.9) * mm});
            skLineSegment(sketch, "E455", {"start": v(-28.67, -33.9) * mm, "end": v(-22.87, -37.44) * mm});
            skLineSegment(sketch, "E456", {"start": v(-22.87, -37.44) * mm, "end": v(-16.56, -41.5) * mm});
            skLineSegment(sketch, "E457", {"start": v(-16.56, -41.5) * mm, "end": v(-12.78, -44.08) * mm});
            skLineSegment(sketch, "E458", {"start": v(-12.78, -44.08) * mm, "end": v(-11.03, -45.23) * mm});
            skLineSegment(sketch, "E459", {"start": v(-11.03, -45.23) * mm, "end": v(-8.7, -46.88) * mm});
            skLineSegment(sketch, "E460", {"start": v(-8.7, -46.88) * mm, "end": v(-6.62, -48.77) * mm});
            skLineSegment(sketch, "E461", {"start": v(-6.62, -48.77) * mm, "end": v(-5.53, -49.74) * mm});
            skLineSegment(sketch, "E462", {"start": v(-5.53, -49.74) * mm, "end": v(-2.22, -51.8) * mm});
            skLineSegment(sketch, "E463", {"start": v(-2.22, -51.8) * mm, "end": v(3.17, -54.87) * mm});
            skLineSegment(sketch, "E464", {"start": v(3.17, -54.87) * mm, "end": v(3.97, -55.21) * mm});
            skLineSegment(sketch, "E465", {"start": v(3.97, -55.21) * mm, "end": v(6.06, -55.82) * mm});
            skLineSegment(sketch, "E466", {"start": v(6.06, -55.82) * mm, "end": v(7.7, -56.05) * mm});
            skLineSegment(sketch, "E467", {"start": v(7.7, -56.05) * mm, "end": v(12.15, -55.96) * mm});
            skLineSegment(sketch, "E468", {"start": v(12.15, -55.96) * mm, "end": v(12.7, -55.92) * mm});
            skLineSegment(sketch, "E469", {"start": v(37.3, -49.15) * mm, "end": v(36.72, -49.21) * mm});
            skLineSegment(sketch, "E470", {"start": v(36.72, -49.21) * mm, "end": v(35.94, -49.45) * mm});
            skLineSegment(sketch, "E471", {"start": v(35.94, -49.45) * mm, "end": v(35.21, -50.1) * mm});
            skLineSegment(sketch, "E472", {"start": v(35.21, -50.1) * mm, "end": v(34.65, -50.94) * mm});
            skLineSegment(sketch, "E473", {"start": v(34.65, -50.94) * mm, "end": v(34.26, -51.87) * mm});
            skLineSegment(sketch, "E474", {"start": v(34.26, -51.87) * mm, "end": v(34.2, -52) * mm});
            skLineSegment(sketch, "E475", {"start": v(34.2, -52) * mm, "end": v(33.57, -51.79) * mm});
            skLineSegment(sketch, "E476", {"start": v(33.57, -51.79) * mm, "end": v(32.57, -53.1) * mm});
            skLineSegment(sketch, "E477", {"start": v(32.57, -53.1) * mm, "end": v(32.57, -53.6) * mm});
            skLineSegment(sketch, "E478", {"start": v(32.57, -53.6) * mm, "end": v(33.77, -55.3) * mm});
            skLineSegment(sketch, "E479", {"start": v(33.77, -55.3) * mm, "end": v(34.09, -55.64) * mm});
            skLineSegment(sketch, "E480", {"start": v(34.09, -55.64) * mm, "end": v(34.2, -55.48) * mm});
            skLineSegment(sketch, "E481", {"start": v(34.2, -55.48) * mm, "end": v(35.4, -53.97) * mm});
            skLineSegment(sketch, "E482", {"start": v(35.4, -53.97) * mm, "end": v(35.58, -53.69) * mm});
            skLineSegment(sketch, "E483", {"start": v(35.58, -53.69) * mm, "end": v(35.9, -53.13) * mm});
            skLineSegment(sketch, "E484", {"start": v(35.9, -53.13) * mm, "end": v(36.49, -53.46) * mm});
            skLineSegment(sketch, "E485", {"start": v(36.49, -53.46) * mm, "end": v(37.06, -53.41) * mm});
            skLineSegment(sketch, "E486", {"start": v(37.06, -53.41) * mm, "end": v(37.67, -52.8) * mm});
            skLineSegment(sketch, "E487", {"start": v(37.67, -52.8) * mm, "end": v(38.8, -51.3) * mm});
            skLineSegment(sketch, "E488", {"start": v(38.8, -51.3) * mm, "end": v(39.03, -50.8) * mm});
            skLineSegment(sketch, "E489", {"start": v(39.03, -50.8) * mm, "end": v(39.21, -50.03) * mm});
            skLineSegment(sketch, "E490", {"start": v(39.21, -50.03) * mm, "end": v(39.98, -50.26) * mm});
            skLineSegment(sketch, "E491", {"start": v(39.98, -50.26) * mm, "end": v(40.32, -50.09) * mm});
            skLineSegment(sketch, "E492", {"start": v(40.32, -50.09) * mm, "end": v(41.18, -49.23) * mm});
            skLineSegment(sketch, "E493", {"start": v(41.18, -49.23) * mm, "end": v(41.8, -48.63) * mm});
            skLineSegment(sketch, "E494", {"start": v(41.8, -48.63) * mm, "end": v(40.19, -47.43) * mm});
            skLineSegment(sketch, "E495", {"start": v(40.19, -47.43) * mm, "end": v(38.68, -46.3) * mm});
            skLineSegment(sketch, "E496", {"start": v(38.68, -46.3) * mm, "end": v(37.8, -47.36) * mm});
            skLineSegment(sketch, "E497", {"start": v(37.8, -47.36) * mm, "end": v(36.9, -48.44) * mm});
            skLineSegment(sketch, "E498", {"start": v(36.9, -48.44) * mm, "end": v(37.3, -49.15) * mm});
            skLineSegment(sketch, "E499", {"start": v(11.42, -51.32) * mm, "end": v(12.53, -52.5) * mm});
            skLineSegment(sketch, "E500", {"start": v(12.53, -52.5) * mm, "end": v(13.98, -53.69) * mm});
            skLineSegment(sketch, "E501", {"start": v(13.98, -53.69) * mm, "end": v(14.28, -54) * mm});
            skLineSegment(sketch, "E502", {"start": v(14.28, -54) * mm, "end": v(14.72, -54.67) * mm});
            skLineSegment(sketch, "E503", {"start": v(14.72, -54.67) * mm, "end": v(15.15, -54.99) * mm});
            skLineSegment(sketch, "E504", {"start": v(15.15, -54.99) * mm, "end": v(16.62, -55.48) * mm});
            skLineSegment(sketch, "E505", {"start": v(16.62, -55.48) * mm, "end": v(16.82, -55.58) * mm});
            skLineSegment(sketch, "E506", {"start": v(16.82, -55.58) * mm, "end": v(17.8, -56.63) * mm});
            skLineSegment(sketch, "E507", {"start": v(17.8, -56.63) * mm, "end": v(18.38, -57.17) * mm});
            skLineSegment(sketch, "E508", {"start": v(18.38, -57.17) * mm, "end": v(18.78, -57.3) * mm});
            skLineSegment(sketch, "E509", {"start": v(18.78, -57.3) * mm, "end": v(21.12, -57.27) * mm});
            skLineSegment(sketch, "E510", {"start": v(21.12, -57.27) * mm, "end": v(21.51, -57.32) * mm});
            skLineSegment(sketch, "E511", {"start": v(21.51, -57.32) * mm, "end": v(22.62, -57.65) * mm});
            skLineSegment(sketch, "E512", {"start": v(22.62, -57.65) * mm, "end": v(23.19, -57.62) * mm});
            skLineSegment(sketch, "E513", {"start": v(23.19, -57.62) * mm, "end": v(24.73, -57.34) * mm});
            skLineSegment(sketch, "E514", {"start": v(24.73, -57.34) * mm, "end": v(25.94, -57.14) * mm});
            skLineSegment(sketch, "E515", {"start": v(25.94, -57.14) * mm, "end": v(26.13, -57.03) * mm});
            skLineSegment(sketch, "E516", {"start": v(26.13, -57.03) * mm, "end": v(25.85, -56.83) * mm});
            skLineSegment(sketch, "E517", {"start": v(25.85, -56.83) * mm, "end": v(23.88, -55.58) * mm});
            skLineSegment(sketch, "E518", {"start": v(23.88, -55.58) * mm, "end": v(23.07, -55.26) * mm});
            skLineSegment(sketch, "E519", {"start": v(23.07, -55.26) * mm, "end": v(17.9, -54.16) * mm});
            skLineSegment(sketch, "E520", {"start": v(17.9, -54.16) * mm, "end": v(17.48, -54.01) * mm});
            skLineSegment(sketch, "E521", {"start": v(17.48, -54.01) * mm, "end": v(14.58, -52.58) * mm});
            skLineSegment(sketch, "E522", {"start": v(14.58, -52.58) * mm, "end": v(14.26, -52.38) * mm});
            skLineSegment(sketch, "E523", {"start": v(14.26, -52.38) * mm, "end": v(12.3, -50.9) * mm});
            skLineSegment(sketch, "E524", {"start": v(12.3, -50.9) * mm, "end": v(11.9, -50.62) * mm});
            skLineSegment(sketch, "E525", {"start": v(11.9, -50.62) * mm, "end": v(11.42, -51.32) * mm});
            skLineSegment(sketch, "E526", {"start": v(45.88, -38.26) * mm, "end": v(45.53, -37.49) * mm});
            skLineSegment(sketch, "E527", {"start": v(45.53, -37.49) * mm, "end": v(45.54, -37) * mm});
            skLineSegment(sketch, "E528", {"start": v(45.54, -37) * mm, "end": v(46.11, -35.49) * mm});
            skLineSegment(sketch, "E529", {"start": v(46.11, -35.49) * mm, "end": v(46.08, -35.12) * mm});
            skLineSegment(sketch, "E530", {"start": v(46.08, -35.12) * mm, "end": v(45.78, -34.09) * mm});
            skLineSegment(sketch, "E531", {"start": v(45.78, -34.09) * mm, "end": v(45.28, -32.93) * mm});
            skLineSegment(sketch, "E532", {"start": v(45.28, -32.93) * mm, "end": v(44.98, -32.5) * mm});
            skLineSegment(sketch, "E533", {"start": v(44.98, -32.5) * mm, "end": v(44.25, -30.95) * mm});
            skLineSegment(sketch, "E534", {"start": v(44.25, -30.95) * mm, "end": v(43.67, -30.19) * mm});
            skLineSegment(sketch, "E535", {"start": v(43.67, -30.19) * mm, "end": v(42.73, -29.04) * mm});
            skLineSegment(sketch, "E536", {"start": v(42.73, -29.04) * mm, "end": v(42.42, -28.57) * mm});
            skLineSegment(sketch, "E537", {"start": v(42.42, -28.57) * mm, "end": v(42.23, -28.37) * mm});
            skLineSegment(sketch, "E538", {"start": v(42.23, -28.37) * mm, "end": v(41.05, -27.78) * mm});
            skLineSegment(sketch, "E539", {"start": v(41.05, -27.78) * mm, "end": v(41.18, -28.26) * mm});
            skLineSegment(sketch, "E540", {"start": v(41.18, -28.26) * mm, "end": v(41.9, -30.48) * mm});
            skLineSegment(sketch, "E541", {"start": v(41.9, -30.48) * mm, "end": v(42.92, -34.33) * mm});
            skLineSegment(sketch, "E542", {"start": v(42.92, -34.33) * mm, "end": v(43.6, -38.91) * mm});
            skLineSegment(sketch, "E543", {"start": v(43.6, -38.91) * mm, "end": v(43.71, -39.37) * mm});
            skLineSegment(sketch, "E544", {"start": v(43.71, -39.37) * mm, "end": v(44.43, -41.46) * mm});
            skLineSegment(sketch, "E545", {"start": v(44.43, -41.46) * mm, "end": v(44.55, -41.71) * mm});
            skLineSegment(sketch, "E546", {"start": v(44.55, -41.71) * mm, "end": v(45.88, -38.26) * mm});
            skLineSegment(sketch, "E547", {"start": v(46.51, -51.2) * mm, "end": v(46.5, -51.63) * mm});
            skLineSegment(sketch, "E548", {"start": v(46.5, -51.63) * mm, "end": v(46.52, -53.2) * mm});
            skLineSegment(sketch, "E549", {"start": v(46.52, -53.2) * mm, "end": v(46.4, -54.14) * mm});
            skLineSegment(sketch, "E550", {"start": v(46.4, -54.14) * mm, "end": v(46, -55.59) * mm});
            skLineSegment(sketch, "E551", {"start": v(46, -55.59) * mm, "end": v(45.91, -56) * mm});
            skLineSegment(sketch, "E552", {"start": v(45.91, -56) * mm, "end": v(46.03, -56.04) * mm});
            skLineSegment(sketch, "E553", {"start": v(46.03, -56.04) * mm, "end": v(48.97, -56.3) * mm});
            skLineSegment(sketch, "E554", {"start": v(48.97, -56.3) * mm, "end": v(49.34, -56.18) * mm});
            skLineSegment(sketch, "E555", {"start": v(49.34, -56.18) * mm, "end": v(51.7, -54.34) * mm});
            skLineSegment(sketch, "E556", {"start": v(51.7, -54.34) * mm, "end": v(51.89, -54.18) * mm});
            skLineSegment(sketch, "E557", {"start": v(51.89, -54.18) * mm, "end": v(51.81, -54.1) * mm});
            skLineSegment(sketch, "E558", {"start": v(51.81, -54.1) * mm, "end": v(46.51, -51.2) * mm});
            skLineSegment(sketch, "E559", {"start": v(31.67, -40.7) * mm, "end": v(32.5, -41.92) * mm});
            skLineSegment(sketch, "E560", {"start": v(32.5, -41.92) * mm, "end": v(33.64, -42.97) * mm});
            skLineSegment(sketch, "E561", {"start": v(33.64, -42.97) * mm, "end": v(34.5, -43.5) * mm});
            skLineSegment(sketch, "E562", {"start": v(34.5, -43.5) * mm, "end": v(33.84, -42.15) * mm});
            skLineSegment(sketch, "E563", {"start": v(33.84, -42.15) * mm, "end": v(34.35, -42.06) * mm});
            skLineSegment(sketch, "E564", {"start": v(34.35, -42.06) * mm, "end": v(34.63, -41.94) * mm});
            skLineSegment(sketch, "E565", {"start": v(34.63, -41.94) * mm, "end": v(35.13, -41.52) * mm});
            skLineSegment(sketch, "E566", {"start": v(35.13, -41.52) * mm, "end": v(35.28, -41.17) * mm});
            skLineSegment(sketch, "E567", {"start": v(35.28, -41.17) * mm, "end": v(35.23, -40.4) * mm});
            skLineSegment(sketch, "E568", {"start": v(35.23, -40.4) * mm, "end": v(34.98, -39.9) * mm});
            skLineSegment(sketch, "E569", {"start": v(34.98, -39.9) * mm, "end": v(34.34, -39.34) * mm});
            skLineSegment(sketch, "E570", {"start": v(34.34, -39.34) * mm, "end": v(35.52, -38.23) * mm});
            skLineSegment(sketch, "E571", {"start": v(35.52, -38.23) * mm, "end": v(35.9, -37.56) * mm});
            skLineSegment(sketch, "E572", {"start": v(35.9, -37.56) * mm, "end": v(35.9, -37.42) * mm});
            skLineSegment(sketch, "E573", {"start": v(35.9, -37.42) * mm, "end": v(35.53, -36.88) * mm});
            skLineSegment(sketch, "E574", {"start": v(35.53, -36.88) * mm, "end": v(34.21, -37.8) * mm});
            skLineSegment(sketch, "E575", {"start": v(34.21, -37.8) * mm, "end": v(32.76, -39.02) * mm});
            skLineSegment(sketch, "E576", {"start": v(32.76, -39.02) * mm, "end": v(31.67, -40.7) * mm});
            skLineSegment(sketch, "E577", {"start": v(26.22, -44.48) * mm, "end": v(25.87, -44.7) * mm});
            skLineSegment(sketch, "E578", {"start": v(25.87, -44.7) * mm, "end": v(24.38, -45.77) * mm});
            skLineSegment(sketch, "E579", {"start": v(24.38, -45.77) * mm, "end": v(23.82, -46.3) * mm});
            skLineSegment(sketch, "E580", {"start": v(23.82, -46.3) * mm, "end": v(22.8, -47.34) * mm});
            skLineSegment(sketch, "E581", {"start": v(22.8, -47.34) * mm, "end": v(22.4, -48.45) * mm});
            skLineSegment(sketch, "E582", {"start": v(22.4, -48.45) * mm, "end": v(23.22, -49.62) * mm});
            skLineSegment(sketch, "E583", {"start": v(23.22, -49.62) * mm, "end": v(24.4, -50.69) * mm});
            skLineSegment(sketch, "E584", {"start": v(24.4, -50.69) * mm, "end": v(25.15, -51.14) * mm});
            skLineSegment(sketch, "E585", {"start": v(25.15, -51.14) * mm, "end": v(24.49, -49.78) * mm});
            skLineSegment(sketch, "E586", {"start": v(24.49, -49.78) * mm, "end": v(25.35, -49.59) * mm});
            skLineSegment(sketch, "E587", {"start": v(25.35, -49.59) * mm, "end": v(25.8, -49.12) * mm});
            skLineSegment(sketch, "E588", {"start": v(25.8, -49.12) * mm, "end": v(25.92, -48.48) * mm});
            skLineSegment(sketch, "E589", {"start": v(25.92, -48.48) * mm, "end": v(25.78, -47.94) * mm});
            skLineSegment(sketch, "E590", {"start": v(25.78, -47.94) * mm, "end": v(25.02, -46.93) * mm});
            skLineSegment(sketch, "E591", {"start": v(25.02, -46.93) * mm, "end": v(25.27, -46.68) * mm});
            skLineSegment(sketch, "E592", {"start": v(25.27, -46.68) * mm, "end": v(26.25, -45.77) * mm});
            skLineSegment(sketch, "E593", {"start": v(26.25, -45.77) * mm, "end": v(26.43, -45.05) * mm});
            skLineSegment(sketch, "E594", {"start": v(26.43, -45.05) * mm, "end": v(26.22, -44.48) * mm});
            skLineSegment(sketch, "E595", {"start": v(35.9, -46.94) * mm, "end": v(35.26, -46.3) * mm});
            skLineSegment(sketch, "E596", {"start": v(35.26, -46.3) * mm, "end": v(34.66, -45.98) * mm});
            skLineSegment(sketch, "E597", {"start": v(34.66, -45.98) * mm, "end": v(33.94, -45.81) * mm});
            skLineSegment(sketch, "E598", {"start": v(33.94, -45.81) * mm, "end": v(33.3, -45.96) * mm});
            skLineSegment(sketch, "E599", {"start": v(33.3, -45.96) * mm, "end": v(32.56, -46.66) * mm});
            skLineSegment(sketch, "E600", {"start": v(32.56, -46.66) * mm, "end": v(31.85, -47.41) * mm});
            skLineSegment(sketch, "E601", {"start": v(31.85, -47.41) * mm, "end": v(31.44, -48.42) * mm});
            skLineSegment(sketch, "E602", {"start": v(31.44, -48.42) * mm, "end": v(31.63, -49.49) * mm});
            skLineSegment(sketch, "E603", {"start": v(31.63, -49.49) * mm, "end": v(31.76, -49.62) * mm});
            skLineSegment(sketch, "E604", {"start": v(31.76, -49.62) * mm, "end": v(32.43, -49.86) * mm});
            skLineSegment(sketch, "E605", {"start": v(32.43, -49.86) * mm, "end": v(33.23, -49.5) * mm});
            skLineSegment(sketch, "E606", {"start": v(33.23, -49.5) * mm, "end": v(33.9, -49.15) * mm});
            skLineSegment(sketch, "E607", {"start": v(33.9, -49.15) * mm, "end": v(34.79, -48.68) * mm});
            skLineSegment(sketch, "E608", {"start": v(34.79, -48.68) * mm, "end": v(35.9, -46.94) * mm});
            skLineSegment(sketch, "E609", {"start": v(46.47, -58.8) * mm, "end": v(46.1, -58.68) * mm});
            skLineSegment(sketch, "E610", {"start": v(46.1, -58.68) * mm, "end": v(43.95, -58.08) * mm});
            skLineSegment(sketch, "E611", {"start": v(43.95, -58.08) * mm, "end": v(43.58, -58.03) * mm});
            skLineSegment(sketch, "E612", {"start": v(43.58, -58.03) * mm, "end": v(42.78, -58.07) * mm});
            skLineSegment(sketch, "E613", {"start": v(42.78, -58.07) * mm, "end": v(42.1, -58.42) * mm});
            skLineSegment(sketch, "E614", {"start": v(42.1, -58.42) * mm, "end": v(42.04, -58.53) * mm});
            skLineSegment(sketch, "E615", {"start": v(42.04, -58.53) * mm, "end": v(42.03, -59.36) * mm});
            skLineSegment(sketch, "E616", {"start": v(42.03, -59.36) * mm, "end": v(42.6, -62) * mm});
            skLineSegment(sketch, "E617", {"start": v(42.6, -62) * mm, "end": v(42.64, -62.04) * mm});
            skLineSegment(sketch, "E618", {"start": v(42.64, -62.04) * mm, "end": v(43.11, -61.56) * mm});
            skLineSegment(sketch, "E619", {"start": v(43.11, -61.56) * mm, "end": v(44.07, -60.74) * mm});
            skLineSegment(sketch, "E620", {"start": v(44.07, -60.74) * mm, "end": v(45.38, -60.08) * mm});
            skLineSegment(sketch, "E621", {"start": v(45.38, -60.08) * mm, "end": v(45.55, -59.97) * mm});
            skLineSegment(sketch, "E622", {"start": v(45.55, -59.97) * mm, "end": v(46.47, -58.8) * mm});
            skLineSegment(sketch, "E623", {"start": v(37.12, -60.84) * mm, "end": v(37.2, -62.99) * mm});
            skLineSegment(sketch, "E624", {"start": v(37.2, -62.99) * mm, "end": v(37.41, -65.14) * mm});
            skLineSegment(sketch, "E625", {"start": v(37.41, -65.14) * mm, "end": v(39.44, -63.62) * mm});
            skLineSegment(sketch, "E626", {"start": v(39.44, -63.62) * mm, "end": v(39.58, -63.29) * mm});
            skLineSegment(sketch, "E627", {"start": v(39.58, -63.29) * mm, "end": v(39.83, -61.18) * mm});
            skLineSegment(sketch, "E628", {"start": v(39.83, -61.18) * mm, "end": v(39.85, -60.9) * mm});
            skLineSegment(sketch, "E629", {"start": v(39.85, -60.9) * mm, "end": v(37.12, -60.84) * mm});
            skLineSegment(sketch, "E630", {"start": v(37.17, -38.47) * mm, "end": v(37.1, -38.48) * mm});
            skLineSegment(sketch, "E631", {"start": v(37.1, -38.48) * mm, "end": v(37.09, -38.82) * mm});
            skLineSegment(sketch, "E632", {"start": v(37.09, -38.82) * mm, "end": v(37.1, -39.81) * mm});
            skLineSegment(sketch, "E633", {"start": v(37.1, -39.81) * mm, "end": v(36.72, -42.02) * mm});
            skLineSegment(sketch, "E634", {"start": v(36.72, -42.02) * mm, "end": v(36.03, -43.19) * mm});
            skLineSegment(sketch, "E635", {"start": v(36.03, -43.19) * mm, "end": v(35.78, -44) * mm});
            skLineSegment(sketch, "E636", {"start": v(35.78, -44) * mm, "end": v(36.58, -44.08) * mm});
            skLineSegment(sketch, "E637", {"start": v(36.58, -44.08) * mm, "end": v(36.8, -44.01) * mm});
            skLineSegment(sketch, "E638", {"start": v(36.8, -44.01) * mm, "end": v(37.86, -43.35) * mm});
            skLineSegment(sketch, "E639", {"start": v(37.86, -43.35) * mm, "end": v(38.02, -43.13) * mm});
            skLineSegment(sketch, "E640", {"start": v(38.02, -43.13) * mm, "end": v(38.35, -41.65) * mm});
            skLineSegment(sketch, "E641", {"start": v(38.35, -41.65) * mm, "end": v(38.33, -40.97) * mm});
            skLineSegment(sketch, "E642", {"start": v(38.33, -40.97) * mm, "end": v(38.1, -40.1) * mm});
            skLineSegment(sketch, "E643", {"start": v(38.1, -40.1) * mm, "end": v(37.17, -38.47) * mm});
            skLineSegment(sketch, "E644", {"start": v(28.27, -46.02) * mm, "end": v(28.17, -46.02) * mm});
            skLineSegment(sketch, "E645", {"start": v(28.17, -46.02) * mm, "end": v(28.2, -46.22) * mm});
            skLineSegment(sketch, "E646", {"start": v(28.2, -46.22) * mm, "end": v(27.95, -48.8) * mm});
            skLineSegment(sketch, "E647", {"start": v(27.95, -48.8) * mm, "end": v(27.8, -49.36) * mm});
            skLineSegment(sketch, "E648", {"start": v(27.8, -49.36) * mm, "end": v(27.42, -50.04) * mm});
            skLineSegment(sketch, "E649", {"start": v(27.42, -50.04) * mm, "end": v(27.13, -50.23) * mm});
            skLineSegment(sketch, "E650", {"start": v(27.13, -50.23) * mm, "end": v(26.65, -50.34) * mm});
            skLineSegment(sketch, "E651", {"start": v(26.65, -50.34) * mm, "end": v(26.42, -51.3) * mm});
            skLineSegment(sketch, "E652", {"start": v(26.42, -51.3) * mm, "end": v(27.76, -51.32) * mm});
            skLineSegment(sketch, "E653", {"start": v(27.76, -51.32) * mm, "end": v(27.88, -51.3) * mm});
            skLineSegment(sketch, "E654", {"start": v(27.88, -51.3) * mm, "end": v(29.03, -50.22) * mm});
            skLineSegment(sketch, "E655", {"start": v(29.03, -50.22) * mm, "end": v(29.34, -49.19) * mm});
            skLineSegment(sketch, "E656", {"start": v(29.34, -49.19) * mm, "end": v(29.1, -47.99) * mm});
            skLineSegment(sketch, "E657", {"start": v(29.1, -47.99) * mm, "end": v(28.98, -47.7) * mm});
            skLineSegment(sketch, "E658", {"start": v(28.98, -47.7) * mm, "end": v(28.27, -46.02) * mm});
            skLineSegment(sketch, "E659", {"start": v(60.84, -46.36) * mm, "end": v(59.61, -45.36) * mm});
            skLineSegment(sketch, "E660", {"start": v(59.61, -45.36) * mm, "end": v(59.44, -45.3) * mm});
            skLineSegment(sketch, "E661", {"start": v(59.44, -45.3) * mm, "end": v(58.68, -45.2) * mm});
            skLineSegment(sketch, "E662", {"start": v(58.68, -45.2) * mm, "end": v(58.25, -46.2) * mm});
            skLineSegment(sketch, "E663", {"start": v(58.25, -46.2) * mm, "end": v(58.3, -46.82) * mm});
            skLineSegment(sketch, "E664", {"start": v(58.3, -46.82) * mm, "end": v(58.96, -47.8) * mm});
            skLineSegment(sketch, "E665", {"start": v(58.96, -47.8) * mm, "end": v(59.11, -47.97) * mm});
            skLineSegment(sketch, "E666", {"start": v(59.11, -47.97) * mm, "end": v(60.84, -46.36) * mm});
            skLineSegment(sketch, "E667", {"start": v(62.8, -44.58) * mm, "end": v(62.7, -44.47) * mm});
            skLineSegment(sketch, "E668", {"start": v(62.7, -44.47) * mm, "end": v(61.47, -43.62) * mm});
            skLineSegment(sketch, "E669", {"start": v(61.47, -43.62) * mm, "end": v(60.79, -43.5) * mm});
            skLineSegment(sketch, "E670", {"start": v(60.79, -43.5) * mm, "end": v(60.52, -43.92) * mm});
            skLineSegment(sketch, "E671", {"start": v(60.52, -43.92) * mm, "end": v(60.48, -44) * mm});
            skLineSegment(sketch, "E672", {"start": v(60.48, -44) * mm, "end": v(60.5, -44.42) * mm});
            skLineSegment(sketch, "E673", {"start": v(60.5, -44.42) * mm, "end": v(60.82, -44.95) * mm});
            skLineSegment(sketch, "E674", {"start": v(60.82, -44.95) * mm, "end": v(61.48, -45.83) * mm});
            skLineSegment(sketch, "E675", {"start": v(61.48, -45.83) * mm, "end": v(62.8, -44.58) * mm});
            skLineSegment(sketch, "E676", {"start": v(39.55, -57.45) * mm, "end": v(36.7, -58.98) * mm});
            skLineSegment(sketch, "E677", {"start": v(36.7, -58.98) * mm, "end": v(38.2, -59.2) * mm});
            skLineSegment(sketch, "E678", {"start": v(38.2, -59.2) * mm, "end": v(39.72, -59.08) * mm});
            skLineSegment(sketch, "E679", {"start": v(39.72, -59.08) * mm, "end": v(39.55, -57.45) * mm});
            skLineSegment(sketch, "E680", {"start": v(28.82, -70.13) * mm, "end": v(28.05, -69.1) * mm});
            skLineSegment(sketch, "E681", {"start": v(28.05, -69.1) * mm, "end": v(27.23, -68.47) * mm});
            skLineSegment(sketch, "E682", {"start": v(27.23, -68.47) * mm, "end": v(27.1, -69.76) * mm});
            skLineSegment(sketch, "E683", {"start": v(27.1, -69.76) * mm, "end": v(27.37, -71.02) * mm});
            skLineSegment(sketch, "E684", {"start": v(27.37, -71.02) * mm, "end": v(28.82, -70.13) * mm});
            skLineSegment(sketch, "E685", {"start": v(29.6, -69.57) * mm, "end": v(31.58, -68.7) * mm});
            skLineSegment(sketch, "E686", {"start": v(31.58, -68.7) * mm, "end": v(30.32, -67.87) * mm});
            skLineSegment(sketch, "E687", {"start": v(30.32, -67.87) * mm, "end": v(30.03, -67.9) * mm});
            skLineSegment(sketch, "E688", {"start": v(30.03, -67.9) * mm, "end": v(29.33, -68.42) * mm});
            skLineSegment(sketch, "E689", {"start": v(29.33, -68.42) * mm, "end": v(29.6, -69.57) * mm});
            skLineSegment(sketch, "E690", {"start": v(43.52, -55.23) * mm, "end": v(43.58, -55.17) * mm});
            skLineSegment(sketch, "E691", {"start": v(43.58, -55.17) * mm, "end": v(44.32, -53.08) * mm});
            skLineSegment(sketch, "E692", {"start": v(44.32, -53.08) * mm, "end": v(44.52, -52.12) * mm});
            skLineSegment(sketch, "E693", {"start": v(44.52, -52.12) * mm, "end": v(42.79, -53.84) * mm});
            skLineSegment(sketch, "E694", {"start": v(42.79, -53.84) * mm, "end": v(43.52, -55.23) * mm});
            skLineSegment(sketch, "E695", {"start": v(25.33, -70.95) * mm, "end": v(25.5, -71.72) * mm});
            skLineSegment(sketch, "E696", {"start": v(25.5, -71.72) * mm, "end": v(26.4, -71.38) * mm});
            skLineSegment(sketch, "E697", {"start": v(26.4, -71.38) * mm, "end": v(25.9, -70.85) * mm});
            skLineSegment(sketch, "E698", {"start": v(25.9, -70.85) * mm, "end": v(25.33, -70.95) * mm});
            skSolve(sketch);
        }
        {
            var Q0;
            {var subQ82=sQuery(id+"F0.wireOp",EDGE,"E4.trimOffspring");Q0=makeQuery(id+"F0.imprint","IMPRINT",FACE,{"disambiguationData":[TD([[makeQuery(id+"F0.imprint","IMPRINT",EDGE,{"derivedFrom":subQ82}),-1.0]])]});}
            extrude(context, id + "F2", {"entities" : qUnion([Q0]), "endBound" : BoundingType.SYMMETRIC, "depth" : 2.03 * mm});
        }
        {
            var Q0;
            Q0=makeQuery(id+"F0.imprint","IMPRINT",FACE,{"disambiguationData":[TD([[makeQuery(id+"F0.imprint","IMPRINT",EDGE,{"derivedFrom":sQuery(id+"F0.wireOp",EDGE,"E25")}),1.0]])]});
            var Q1;
            {var subQ0=sQuery(id+"F0.wireOp",EDGE,"E24.4.0");Q1=makeQuery(id+"F0.imprint","IMPRINT",FACE,{"disambiguationData":[TD([[makeQuery(id+"F0.imprint","IMPRINT",EDGE,{"derivedFrom":subQ0}),-1.0]])]});}
            var Q2;
            {var subQ0=sQuery(id+"F0.wireOp",EDGE,"E24.3.0");Q2=makeQuery(id+"F0.imprint","IMPRINT",FACE,{"disambiguationData":[TD([[makeQuery(id+"F0.imprint","IMPRINT",EDGE,{"derivedFrom":subQ0}),-1.0]])]});}
            var Q3;
            {var subQ0=sQuery(id+"F0.wireOp",EDGE,"E24.2.0");Q3=makeQuery(id+"F0.imprint","IMPRINT",FACE,{"disambiguationData":[TD([[makeQuery(id+"F0.imprint","IMPRINT",EDGE,{"derivedFrom":subQ0}),-1.0]])]});}
            var Q4;
            {var subQ0=sQuery(id+"F0.wireOp",EDGE,"E24.1.0");Q4=makeQuery(id+"F0.imprint","IMPRINT",FACE,{"disambiguationData":[TD([[makeQuery(id+"F0.imprint","IMPRINT",EDGE,{"derivedFrom":subQ0}),-1.0]])]});}
            var Q5;
            Q5=makeQuery(id+"F0.imprint","IMPRINT",FACE,{"disambiguationData":[TD([[makeQuery(id+"F0.imprint","IMPRINT",EDGE,{"derivedFrom":sQuery(id+"F0.wireOp",EDGE,"E16")}),-1.0]])]});
            var Q6;
            {var subQ0=sQuery(id+"F0.wireOp",EDGE,"E26");var subQ1=sQuery(id+"F0.wireOp",EDGE,"E24.4.1");var subQ2=makeQuery(id+"F0.imprint","INTERSECT",VERTEX,{"derivedFrom":[subQ1,subQ0]});Q6=makeQuery(id+"F0.imprint","IMPRINT",FACE,{"disambiguationData":[TD([[makeQuery(id+"F0.imprint","IMPRINT",EDGE,{"disambiguationData":[TD([[subQ2,-1.0]])],"derivedFrom":subQ1}),1.0]])]});}
            var Q7;
            {var subQ0=sQuery(id+"F0.wireOp",EDGE,"E26");var subQ1=sQuery(id+"F0.wireOp",EDGE,"E24.3.4");var subQ2=makeQuery(id+"F0.imprint","INTERSECT",VERTEX,{"derivedFrom":[subQ1,subQ0]});Q7=makeQuery(id+"F0.imprint","IMPRINT",FACE,{"disambiguationData":[TD([[makeQuery(id+"F0.imprint","IMPRINT",EDGE,{"disambiguationData":[TD([[subQ2,-1.0]])],"derivedFrom":subQ1}),1.0]])]});}
            var Q8;
            {var subQ1=sQuery(id+"F0.wireOp",EDGE,"E24.4.2");Q8=makeQuery(id+"F0.imprint","IMPRINT",FACE,{"disambiguationData":[TD([[makeQuery(id+"F0.imprint","IMPRINT",EDGE,{"derivedFrom":subQ1}),-1.0]])]});}
            var Q9;
            {var subQ0=sQuery(id+"F0.wireOp",EDGE,"E26");var subQ1=sQuery(id+"F0.wireOp",EDGE,"E17");var subQ2=makeQuery(id+"F0.imprint","INTERSECT",VERTEX,{"derivedFrom":[subQ1,subQ0]});Q9=makeQuery(id+"F0.imprint","IMPRINT",FACE,{"disambiguationData":[TD([[makeQuery(id+"F0.imprint","IMPRINT",EDGE,{"disambiguationData":[TD([[subQ2,-1.0]])],"derivedFrom":subQ1}),-1.0]])]});}
            var Q10;
            {var subQ0=sQuery(id+"F0.wireOp",EDGE,"E18");Q10=makeQuery(id+"F0.imprint","IMPRINT",FACE,{"disambiguationData":[TD([[makeQuery(id+"F0.imprint","IMPRINT",EDGE,{"derivedFrom":subQ0}),-1.0]])]});}
            var Q11;
            {var subQ0=sQuery(id+"F0.wireOp",EDGE,"E26");var subQ1=sQuery(id+"F0.wireOp",EDGE,"E24.4.4");var subQ2=makeQuery(id+"F0.imprint","INTERSECT",VERTEX,{"derivedFrom":[subQ1,subQ0]});Q11=makeQuery(id+"F0.imprint","IMPRINT",FACE,{"disambiguationData":[TD([[makeQuery(id+"F0.imprint","IMPRINT",EDGE,{"disambiguationData":[TD([[subQ2,-1.0]])],"derivedFrom":subQ1}),-1.0]])]});}
            var Q12;
            {var subQ0=sQuery(id+"F0.wireOp",EDGE,"E26");var subQ1=sQuery(id+"F0.wireOp",EDGE,"E24.3.4");var subQ2=makeQuery(id+"F0.imprint","INTERSECT",VERTEX,{"derivedFrom":[subQ1,subQ0]});Q12=makeQuery(id+"F0.imprint","IMPRINT",FACE,{"disambiguationData":[TD([[makeQuery(id+"F0.imprint","IMPRINT",EDGE,{"disambiguationData":[TD([[subQ2,-1.0]])],"derivedFrom":subQ1}),-1.0]])]});}
            var Q13;
            {var subQ0=sQuery(id+"F0.wireOp",EDGE,"E26");var subQ1=sQuery(id+"F0.wireOp",EDGE,"E24.3.1");var subQ2=makeQuery(id+"F0.imprint","INTERSECT",VERTEX,{"derivedFrom":[subQ1,subQ0]});Q13=makeQuery(id+"F0.imprint","IMPRINT",FACE,{"disambiguationData":[TD([[makeQuery(id+"F0.imprint","IMPRINT",EDGE,{"disambiguationData":[TD([[subQ2,-1.0]])],"derivedFrom":subQ1}),1.0]])]});}
            var Q14;
            {var subQ1=sQuery(id+"F0.wireOp",EDGE,"E24.3.2");Q14=makeQuery(id+"F0.imprint","IMPRINT",FACE,{"disambiguationData":[TD([[makeQuery(id+"F0.imprint","IMPRINT",EDGE,{"derivedFrom":subQ1}),-1.0]])]});}
            var Q15;
            Q15=makeQuery(id+"F0.imprint","IMPRINT",FACE,{"disambiguationData":[TD([[makeQuery(id+"F0.imprint","IMPRINT",EDGE,{"derivedFrom":sQuery(id+"F0.wireOp",EDGE,"E28")}),1.0]])]});
            var Q16;
            {var subQ2=sQuery(id+"F0.wireOp",EDGE,"E24.2.4");var subQ4=sQuery(id+"F0.wireOp",EDGE,"E26");var subQ5=makeQuery(id+"F0.imprint","INTERSECT",VERTEX,{"derivedFrom":[subQ2,subQ4]});Q16=makeQuery(id+"F0.imprint","IMPRINT",FACE,{"disambiguationData":[TD([[makeQuery(id+"F0.imprint","IMPRINT",EDGE,{"disambiguationData":[TD([[subQ5,-1.0]])],"derivedFrom":subQ2}),1.0]])]});}
            var Q17;
            {var subQ0=sQuery(id+"F0.wireOp",EDGE,"E26");var subQ1=sQuery(id+"F0.wireOp",EDGE,"E24.2.4");var subQ2=makeQuery(id+"F0.imprint","INTERSECT",VERTEX,{"derivedFrom":[subQ1,subQ0]});Q17=makeQuery(id+"F0.imprint","IMPRINT",FACE,{"disambiguationData":[TD([[makeQuery(id+"F0.imprint","IMPRINT",EDGE,{"disambiguationData":[TD([[subQ2,-1.0]])],"derivedFrom":subQ1}),-1.0]])]});}
            var Q18;
            {var subQ0=sQuery(id+"F0.wireOp",EDGE,"E26");var subQ1=sQuery(id+"F0.wireOp",EDGE,"E24.2.1");var subQ2=makeQuery(id+"F0.imprint","INTERSECT",VERTEX,{"derivedFrom":[subQ1,subQ0]});Q18=makeQuery(id+"F0.imprint","IMPRINT",FACE,{"disambiguationData":[TD([[makeQuery(id+"F0.imprint","IMPRINT",EDGE,{"disambiguationData":[TD([[subQ2,-1.0]])],"derivedFrom":subQ1}),1.0]])]});}
            var Q19;
            {var subQ0=sQuery(id+"F0.wireOp",EDGE,"E26");var subQ1=sQuery(id+"F0.wireOp",EDGE,"E24.1.4");var subQ2=makeQuery(id+"F0.imprint","INTERSECT",VERTEX,{"derivedFrom":[subQ1,subQ0]});Q19=makeQuery(id+"F0.imprint","IMPRINT",FACE,{"disambiguationData":[TD([[makeQuery(id+"F0.imprint","IMPRINT",EDGE,{"disambiguationData":[TD([[subQ2,-1.0]])],"derivedFrom":subQ1}),1.0]])]});}
            var Q20;
            {var subQ0=sQuery(id+"F0.wireOp",EDGE,"E26");var subQ1=sQuery(id+"F0.wireOp",EDGE,"E24.1.4");var subQ2=makeQuery(id+"F0.imprint","INTERSECT",VERTEX,{"derivedFrom":[subQ1,subQ0]});Q20=makeQuery(id+"F0.imprint","IMPRINT",FACE,{"disambiguationData":[TD([[makeQuery(id+"F0.imprint","IMPRINT",EDGE,{"disambiguationData":[TD([[subQ2,-1.0]])],"derivedFrom":subQ1}),-1.0]])]});}
            var Q21;
            {var subQ0=sQuery(id+"F0.wireOp",EDGE,"E19");Q21=makeQuery(id+"F0.imprint","IMPRINT",FACE,{"disambiguationData":[TD([[makeQuery(id+"F0.imprint","IMPRINT",EDGE,{"derivedFrom":subQ0}),-1.0]])]});}
            var Q22;
            {var subQ0=sQuery(id+"F0.wireOp",EDGE,"E26");var subQ1=sQuery(id+"F0.wireOp",EDGE,"E24.1.1");var subQ2=makeQuery(id+"F0.imprint","INTERSECT",VERTEX,{"derivedFrom":[subQ1,subQ0]});Q22=makeQuery(id+"F0.imprint","IMPRINT",FACE,{"disambiguationData":[TD([[makeQuery(id+"F0.imprint","IMPRINT",EDGE,{"disambiguationData":[TD([[subQ2,-1.0]])],"derivedFrom":subQ1}),1.0]])]});}
            var Q23;
            {var subQ1=sQuery(id+"F0.wireOp",EDGE,"E24.1.2");Q23=makeQuery(id+"F0.imprint","IMPRINT",FACE,{"disambiguationData":[TD([[makeQuery(id+"F0.imprint","IMPRINT",EDGE,{"derivedFrom":subQ1}),-1.0]])]});}
            var Q24;
            {var subQ1=sQuery(id+"F0.wireOp",EDGE,"E24.2.2");Q24=makeQuery(id+"F0.imprint","IMPRINT",FACE,{"disambiguationData":[TD([[makeQuery(id+"F0.imprint","IMPRINT",EDGE,{"derivedFrom":subQ1}),-1.0]])]});}
            var Q25;
            Q25=qSketchRegion(id+"F1",true);
            extrude(context, id + "F3", {"entities" : qUnion([Q0, Q1, Q2, Q3, Q4, Q5, Q6, Q7, Q8, Q9, Q10, Q11, Q12, Q13, Q14, Q15, Q16, Q17, Q18, Q19, Q20, Q21, Q22, Q23, Q24, Q25]), "operationType" : NewBodyOperationType.ADD, "endBound" : BoundingType.SYMMETRIC, "depth" : 2.67 * mm});
        }
    });
